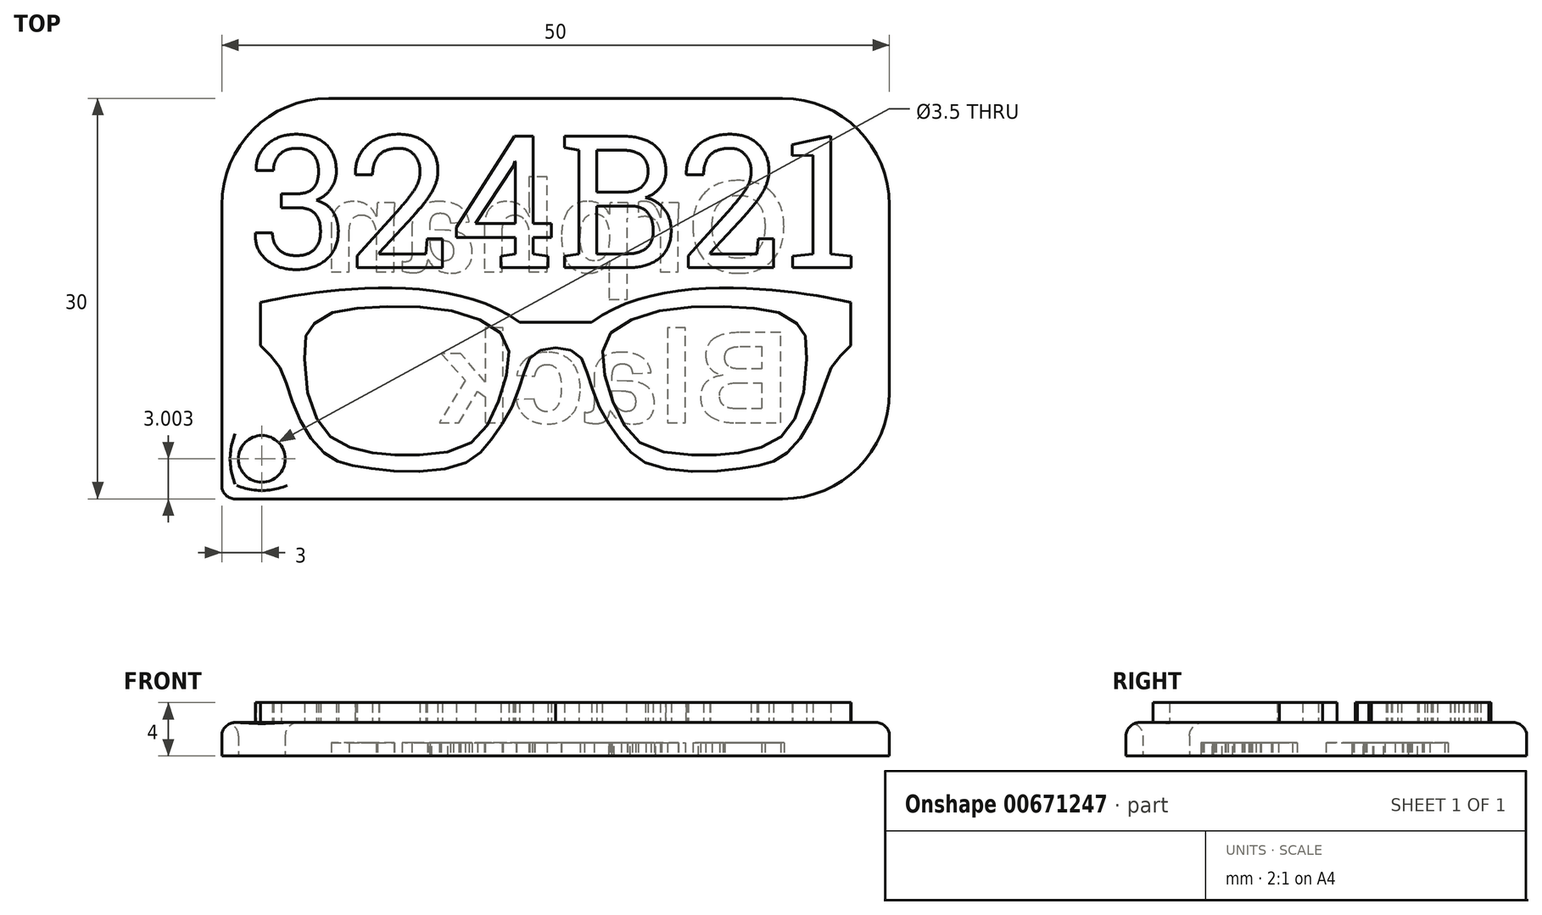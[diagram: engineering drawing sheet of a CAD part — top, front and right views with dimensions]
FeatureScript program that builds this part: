
annotation { "Feature Type Name" : "Feature", "Feature Type Description" : "" }
export const myFeature = defineFeature(function(context is Context, id is Id, definition is map)
    precondition{}
    {
        {
            var Q0;
            Q0=qCreatedBy(makeId("Top.planeOp"),FACE);
            var sketch = newSketch(context, id + "F0", { "sketchPlane" : qUnion([Q0])});
            skFitSpline(sketch, "E0", {"points": [v(2.9, -29.82) * mm, v(22.3, -31.3) * mm], "startDerivative": vector(6.49, 1.44) * mm, "endDerivative": vector(17.58, -13.11) * mm});
            skLineSegment(sketch, "E1", {"start": v(25, -66.67) * mm, "end": v(25, 0) * mm, "construction": true});
            skLineSegment(sketch, "E2", {"start": v(2.9, -29.82) * mm, "end": v(2.9, -33.05) * mm});
            skLineSegment(sketch, "E3", {"start": v(22.3, -31.3) * mm, "end": v(25, -31.3) * mm});
            skFitSpline(sketch, "E4", {"points": [v(2.9, -33.05) * mm, v(4.08, -34.28) * mm, v(4.97, -36.34) * mm, v(6.27, -39.38) * mm, v(8.2, -41.49) * mm, v(10.04, -42.06) * mm, v(13.88, -42.5) * mm, v(18.42, -41.75) * mm, v(20.07, -40.22) * mm, v(21.68, -37.74) * mm, v(22.6, -35.15) * mm, v(23.36, -33.67) * mm, v(25, -33.2) * mm], "startDerivative": vector(14.6, -17.1) * mm, "endDerivative": vector(27.6, 3.2) * mm});
            skFitSpline(sketch, "E5", {"points": [v(14.8, -41.25) * mm, v(17.8, -40.78) * mm, v(19.54, -39.5) * mm, v(20.74, -37.22) * mm, v(21.45, -34.5) * mm, v(21.28, -32.67) * mm, v(19.85, -31.38) * mm, v(16.73, -30.35) * mm, v(12.62, -30.13) * mm, v(9.28, -30.36) * mm, v(7.41, -31) * mm, v(6.45, -32) * mm, v(6.27, -32.53) * mm, v(6.34, -36.02) * mm, v(7.3, -38.87) * mm, v(8.6, -40.24) * mm, v(10.55, -40.94) * mm, v(12.58, -41.22) * mm, v(14.8, -41.25) * mm]});
            skLineSegment(sketch, "E6.MirrorCS", {"start": v(27.7, -31.3) * mm, "end": v(25, -31.3) * mm});
            skLineSegment(sketch, "E7.MirrorCS", {"start": v(47.1, -29.82) * mm, "end": v(47.1, -33.05) * mm});
            skFitSpline(sketch, "E8.MirrorC", {"points": [v(35.2, -41.25) * mm, v(32.2, -40.78) * mm, v(30.46, -39.5) * mm, v(29.26, -37.22) * mm, v(28.55, -34.5) * mm, v(28.72, -32.67) * mm, v(30.15, -31.38) * mm, v(33.27, -30.35) * mm, v(37.38, -30.13) * mm, v(40.72, -30.36) * mm, v(42.59, -31) * mm, v(43.55, -32) * mm, v(43.73, -32.53) * mm, v(43.66, -36.02) * mm, v(42.7, -38.87) * mm, v(41.4, -40.24) * mm, v(39.45, -40.94) * mm, v(37.42, -41.22) * mm, v(35.2, -41.25) * mm]});
            skFitSpline(sketch, "E9.MirrorCS", {"points": [v(47.1, -33.05) * mm, v(45.92, -34.28) * mm, v(45.03, -36.34) * mm, v(43.73, -39.38) * mm, v(41.8, -41.49) * mm, v(39.96, -42.06) * mm, v(36.12, -42.5) * mm, v(31.58, -41.75) * mm, v(29.93, -40.22) * mm, v(28.32, -37.74) * mm, v(27.4, -35.15) * mm, v(26.64, -33.67) * mm, v(25, -33.2) * mm], "startDerivative": vector(-14.6, -17.1) * mm, "endDerivative": vector(-27.6, 3.2) * mm});
            skFitSpline(sketch, "E10.MirrorCS", {"points": [v(47.1, -29.82) * mm, v(27.7, -31.3) * mm], "startDerivative": vector(-6.49, 1.44) * mm, "endDerivative": vector(-17.58, -13.11) * mm});
            skText(sketch, "E11", { "text": "324B21", "fontName": "RobotoSlab-Regular.ttf"});
            skLineSegment(sketch, "E12.bottom", {"start": v(0, -44.54) * mm, "end": v(50, -44.54) * mm});
            skLineSegment(sketch, "E12.top", {"start": v(0, -14.54) * mm, "end": v(50, -14.54) * mm});
            skLineSegment(sketch, "E12.left", {"start": v(0, -44.54) * mm, "end": v(0, -14.54) * mm});
            skLineSegment(sketch, "E12.right", {"start": v(50, -44.54) * mm, "end": v(50, -14.54) * mm});
            skCircle(sketch, "E13", {"center": v(3, -41.54) * mm, "radius": 1.75 * mm});
            const initialGuessF0  = {"E11": [0.002, -0.02722, 1, 0, 0.00998]};
            skSetInitialGuess(sketch, initialGuessF0);
            skSolve(sketch);
        }
        {
            var Q0;
            Q0=makeQuery(id+"F0.imprint","IMPRINT",FACE,{"disambiguationData":[TD([[makeQuery(id+"F0.imprint","IMPRINT",EDGE,{"derivedFrom":sQuery(id+"F0.wireOp",EDGE,"E0")}),1.0]])]});
            var Q1;
            Q1=makeQuery(id+"F0.imprint","IMPRINT",FACE,{"disambiguationData":[TD([[makeQuery(id+"F0.imprint","IMPRINT",EDGE,{"derivedFrom":sQuery(id+"F0.wireOp",EDGE,"E11.sketch_text.stroke-69")}),1.0]])]});
            var Q2;
            Q2=makeQuery(id+"F0.imprint","IMPRINT",FACE,{"disambiguationData":[TD([[makeQuery(id+"F0.imprint","IMPRINT",EDGE,{"derivedFrom":sQuery(id+"F0.wireOp",EDGE,"E11.sketch_text.stroke-97")}),1.0]])]});
            var Q3;
            Q3=makeQuery(id+"F0.imprint","IMPRINT",FACE,{"disambiguationData":[TD([[makeQuery(id+"F0.imprint","IMPRINT",EDGE,{"derivedFrom":sQuery(id+"F0.wireOp",EDGE,"E11.sketch_text.stroke-90")}),1.0]])]});
            var Q4;
            Q4=makeQuery(id+"F0.imprint","IMPRINT",FACE,{"disambiguationData":[TD([[makeQuery(id+"F0.imprint","IMPRINT",EDGE,{"derivedFrom":sQuery(id+"F0.wireOp",EDGE,"E8.MirrorC")}),-1.0]])]});
            var Q5;
            Q5=makeQuery(id+"F0.imprint","IMPRINT",FACE,{"disambiguationData":[TD([[makeQuery(id+"F0.imprint","IMPRINT",EDGE,{"derivedFrom":sQuery(id+"F0.wireOp",EDGE,"E5")}),1.0]])]});
            extrude(context, id + "F1", {"entities" : qUnion([Q0, Q1, Q2, Q3, Q4, Q5]), "depth" : 2.5 * mm, "offsetDistance" : 25 * mm});
        }
        {
            var Q0;
            Q0=makeQuery(id+"F0.imprint","IMPRINT",FACE,{"disambiguationData":[TD([[makeQuery(id+"F0.imprint","IMPRINT",EDGE,{"derivedFrom":sQuery(id+"F0.wireOp",EDGE,"E0")}),-1.0]])]});
            var Q1;
            Q1=makeQuery(id+"F0.imprint","IMPRINT",FACE,{"disambiguationData":[TD([[makeQuery(id+"F0.imprint","IMPRINT",EDGE,{"derivedFrom":sQuery(id+"F0.wireOp",EDGE,"E11.sketch_text.stroke-0")}),-1.0]])]});
            var Q2;
            Q2=makeQuery(id+"F0.imprint","IMPRINT",FACE,{"disambiguationData":[TD([[makeQuery(id+"F0.imprint","IMPRINT",EDGE,{"derivedFrom":sQuery(id+"F0.wireOp",EDGE,"E11.sketch_text.stroke-31")}),-1.0]])]});
            var Q3;
            Q3=makeQuery(id+"F0.imprint","IMPRINT",FACE,{"disambiguationData":[TD([[makeQuery(id+"F0.imprint","IMPRINT",EDGE,{"derivedFrom":sQuery(id+"F0.wireOp",EDGE,"E11.sketch_text.stroke-54")}),-1.0]])]});
            var Q4;
            Q4=makeQuery(id+"F0.imprint","IMPRINT",FACE,{"disambiguationData":[TD([[makeQuery(id+"F0.imprint","IMPRINT",EDGE,{"derivedFrom":sQuery(id+"F0.wireOp",EDGE,"E11.sketch_text.stroke-74")}),-1.0]])]});
            var Q5;
            Q5=makeQuery(id+"F0.imprint","IMPRINT",FACE,{"disambiguationData":[TD([[makeQuery(id+"F0.imprint","IMPRINT",EDGE,{"derivedFrom":sQuery(id+"F0.wireOp",EDGE,"E11.sketch_text.stroke-104")}),-1.0]])]});
            var Q6;
            Q6=makeQuery(id+"F0.imprint","IMPRINT",FACE,{"disambiguationData":[TD([[makeQuery(id+"F0.imprint","IMPRINT",EDGE,{"derivedFrom":sQuery(id+"F0.wireOp",EDGE,"E11.sketch_text.stroke-127")}),-1.0]])]});
            extrude(context, id + "F2", {"entities" : qUnion([Q0, Q1, Q2, Q3, Q4, Q5, Q6]), "operationType" : NewBodyOperationType.ADD, "depth" : 4 * mm, "offsetDistance" : 25 * mm});
        }
        {
            var Q0;
            Q0=makeQuery(id+"F1.opExtrude","SWEPT_EDGE",EDGE,{"disambiguationData":[OSD([sQuery(id+"F0.wireOp",EDGE,"E12.bottom"),sQuery(id+"F0.wireOp",EDGE,"E12.right")])]});
            var Q1;
            Q1=makeQuery(id+"F1.opExtrude","SWEPT_EDGE",EDGE,{"disambiguationData":[OSD([sQuery(id+"F0.wireOp",EDGE,"E12.top"),sQuery(id+"F0.wireOp",EDGE,"E12.right")])]});
            var Q2;
            Q2=makeQuery(id+"F1.opExtrude","SWEPT_EDGE",EDGE,{"disambiguationData":[OSD([sQuery(id+"F0.wireOp",EDGE,"E12.top"),sQuery(id+"F0.wireOp",EDGE,"E12.left")])]});
            fillet(context, id + "F3", {"entities" : qUnion([Q0, Q1, Q2]), "radius" : 8 * mm, "tangentPropagation" : true, "allowEdgeOverflow" : false});
        }
        {
            var Q0;
            Q0=makeQuery(id+"F1.opExtrude","SWEPT_EDGE",EDGE,{"disambiguationData":[OSD([sQuery(id+"F0.wireOp",EDGE,"E12.bottom"),sQuery(id+"F0.wireOp",EDGE,"E12.left")])]});
            var Q1;
            Q1=makeQuery(id+"F1.opExtrude","CAP_EDGE",EDGE,{"disambiguationData":[OSD([sQuery(id+"F0.wireOp",EDGE,"E12.bottom")])],"isStart":false});
            var Q2;
            Q2=makeQuery(id+"F1.opExtrude","CAP_EDGE",EDGE,{"disambiguationData":[OSD([sQuery(id+"F0.wireOp",EDGE,"E12.left")])],"isStart":false});
            var Q3;
            Q3=makeQuery(id+"F1.opExtrude","CAP_EDGE",EDGE,{"disambiguationData":[OSD([sQuery(id+"F0.wireOp",EDGE,"E13")])],"isStart":false});
            var Q4;
            {var subQ0=sQuery(id+"F0.wireOp",EDGE,"E12.left");var subQ1=sQuery(id+"F0.wireOp",EDGE,"E12.top");Q4=makeQuery(id+"F3.opFillet","BLEND_EDGE",EDGE,{"blendedFrom":[makeQuery(id+"F1.opExtrude","SWEPT_EDGE",EDGE,{"disambiguationData":[OSD([subQ1,subQ0])]}),makeQuery(id+"F1.opExtrude","CAP_FACE",FACE,{"disambiguationData":[OSD([sQuery(id+"F0.wireOp",EDGE,"E0"),sQuery(id+"F0.wireOp",EDGE,"E2"),sQuery(id+"F0.wireOp",EDGE,"E3"),sQuery(id+"F0.wireOp",EDGE,"E4"),sQuery(id+"F0.wireOp",EDGE,"E6.MirrorCS"),sQuery(id+"F0.wireOp",EDGE,"E7.MirrorCS"),sQuery(id+"F0.wireOp",EDGE,"E9.MirrorCS"),sQuery(id+"F0.wireOp",EDGE,"E10.MirrorCS"),sQuery(id+"F0.wireOp",EDGE,"E11.sketch_text.stroke-0"),sQuery(id+"F0.wireOp",EDGE,"E11.sketch_text.stroke-1"),sQuery(id+"F0.wireOp",EDGE,"E11.sketch_text.stroke-2"),sQuery(id+"F0.wireOp",EDGE,"E11.sketch_text.stroke-3"),sQuery(id+"F0.wireOp",EDGE,"E11.sketch_text.stroke-4"),sQuery(id+"F0.wireOp",EDGE,"E11.sketch_text.stroke-5"),sQuery(id+"F0.wireOp",EDGE,"E11.sketch_text.stroke-6"),sQuery(id+"F0.wireOp",EDGE,"E11.sketch_text.stroke-7"),sQuery(id+"F0.wireOp",EDGE,"E11.sketch_text.stroke-8"),sQuery(id+"F0.wireOp",EDGE,"E11.sketch_text.stroke-9"),sQuery(id+"F0.wireOp",EDGE,"E11.sketch_text.stroke-10"),sQuery(id+"F0.wireOp",EDGE,"E11.sketch_text.stroke-11"),sQuery(id+"F0.wireOp",EDGE,"E11.sketch_text.stroke-12"),sQuery(id+"F0.wireOp",EDGE,"E11.sketch_text.stroke-13"),sQuery(id+"F0.wireOp",EDGE,"E11.sketch_text.stroke-14"),sQuery(id+"F0.wireOp",EDGE,"E11.sketch_text.stroke-15"),sQuery(id+"F0.wireOp",EDGE,"E11.sketch_text.stroke-16"),sQuery(id+"F0.wireOp",EDGE,"E11.sketch_text.stroke-17"),sQuery(id+"F0.wireOp",EDGE,"E11.sketch_text.stroke-18"),sQuery(id+"F0.wireOp",EDGE,"E11.sketch_text.stroke-19"),sQuery(id+"F0.wireOp",EDGE,"E11.sketch_text.stroke-20"),sQuery(id+"F0.wireOp",EDGE,"E11.sketch_text.stroke-21"),sQuery(id+"F0.wireOp",EDGE,"E11.sketch_text.stroke-22"),sQuery(id+"F0.wireOp",EDGE,"E11.sketch_text.stroke-23"),sQuery(id+"F0.wireOp",EDGE,"E11.sketch_text.stroke-24"),sQuery(id+"F0.wireOp",EDGE,"E11.sketch_text.stroke-25"),sQuery(id+"F0.wireOp",EDGE,"E11.sketch_text.stroke-26"),sQuery(id+"F0.wireOp",EDGE,"E11.sketch_text.stroke-27"),sQuery(id+"F0.wireOp",EDGE,"E11.sketch_text.stroke-28"),sQuery(id+"F0.wireOp",EDGE,"E11.sketch_text.stroke-29"),sQuery(id+"F0.wireOp",EDGE,"E11.sketch_text.stroke-30"),sQuery(id+"F0.wireOp",EDGE,"E11.sketch_text.stroke-31"),sQuery(id+"F0.wireOp",EDGE,"E11.sketch_text.stroke-32"),sQuery(id+"F0.wireOp",EDGE,"E11.sketch_text.stroke-33"),sQuery(id+"F0.wireOp",EDGE,"E11.sketch_text.stroke-34"),sQuery(id+"F0.wireOp",EDGE,"E11.sketch_text.stroke-35"),sQuery(id+"F0.wireOp",EDGE,"E11.sketch_text.stroke-36"),sQuery(id+"F0.wireOp",EDGE,"E11.sketch_text.stroke-37"),sQuery(id+"F0.wireOp",EDGE,"E11.sketch_text.stroke-38"),sQuery(id+"F0.wireOp",EDGE,"E11.sketch_text.stroke-39"),sQuery(id+"F0.wireOp",EDGE,"E11.sketch_text.stroke-40"),sQuery(id+"F0.wireOp",EDGE,"E11.sketch_text.stroke-41"),sQuery(id+"F0.wireOp",EDGE,"E11.sketch_text.stroke-42"),sQuery(id+"F0.wireOp",EDGE,"E11.sketch_text.stroke-43"),sQuery(id+"F0.wireOp",EDGE,"E11.sketch_text.stroke-44"),sQuery(id+"F0.wireOp",EDGE,"E11.sketch_text.stroke-45"),sQuery(id+"F0.wireOp",EDGE,"E11.sketch_text.stroke-46"),sQuery(id+"F0.wireOp",EDGE,"E11.sketch_text.stroke-47"),sQuery(id+"F0.wireOp",EDGE,"E11.sketch_text.stroke-48"),sQuery(id+"F0.wireOp",EDGE,"E11.sketch_text.stroke-49"),sQuery(id+"F0.wireOp",EDGE,"E11.sketch_text.stroke-50"),sQuery(id+"F0.wireOp",EDGE,"E11.sketch_text.stroke-51"),sQuery(id+"F0.wireOp",EDGE,"E11.sketch_text.stroke-52"),sQuery(id+"F0.wireOp",EDGE,"E11.sketch_text.stroke-53"),sQuery(id+"F0.wireOp",EDGE,"E11.sketch_text.stroke-54"),sQuery(id+"F0.wireOp",EDGE,"E11.sketch_text.stroke-55"),sQuery(id+"F0.wireOp",EDGE,"E11.sketch_text.stroke-56"),sQuery(id+"F0.wireOp",EDGE,"E11.sketch_text.stroke-57"),sQuery(id+"F0.wireOp",EDGE,"E11.sketch_text.stroke-58"),sQuery(id+"F0.wireOp",EDGE,"E11.sketch_text.stroke-59"),sQuery(id+"F0.wireOp",EDGE,"E11.sketch_text.stroke-60"),sQuery(id+"F0.wireOp",EDGE,"E11.sketch_text.stroke-61"),sQuery(id+"F0.wireOp",EDGE,"E11.sketch_text.stroke-62"),sQuery(id+"F0.wireOp",EDGE,"E11.sketch_text.stroke-63"),sQuery(id+"F0.wireOp",EDGE,"E11.sketch_text.stroke-64"),sQuery(id+"F0.wireOp",EDGE,"E11.sketch_text.stroke-65"),sQuery(id+"F0.wireOp",EDGE,"E11.sketch_text.stroke-66"),sQuery(id+"F0.wireOp",EDGE,"E11.sketch_text.stroke-67"),sQuery(id+"F0.wireOp",EDGE,"E11.sketch_text.stroke-68"),sQuery(id+"F0.wireOp",EDGE,"E11.sketch_text.stroke-74"),sQuery(id+"F0.wireOp",EDGE,"E11.sketch_text.stroke-75"),sQuery(id+"F0.wireOp",EDGE,"E11.sketch_text.stroke-76"),sQuery(id+"F0.wireOp",EDGE,"E11.sketch_text.stroke-77"),sQuery(id+"F0.wireOp",EDGE,"E11.sketch_text.stroke-78"),sQuery(id+"F0.wireOp",EDGE,"E11.sketch_text.stroke-79"),sQuery(id+"F0.wireOp",EDGE,"E11.sketch_text.stroke-80"),sQuery(id+"F0.wireOp",EDGE,"E11.sketch_text.stroke-81"),sQuery(id+"F0.wireOp",EDGE,"E11.sketch_text.stroke-82"),sQuery(id+"F0.wireOp",EDGE,"E11.sketch_text.stroke-83"),sQuery(id+"F0.wireOp",EDGE,"E11.sketch_text.stroke-84"),sQuery(id+"F0.wireOp",EDGE,"E11.sketch_text.stroke-85"),sQuery(id+"F0.wireOp",EDGE,"E11.sketch_text.stroke-86"),sQuery(id+"F0.wireOp",EDGE,"E11.sketch_text.stroke-87"),sQuery(id+"F0.wireOp",EDGE,"E11.sketch_text.stroke-88"),sQuery(id+"F0.wireOp",EDGE,"E11.sketch_text.stroke-89"),sQuery(id+"F0.wireOp",EDGE,"E11.sketch_text.stroke-104"),sQuery(id+"F0.wireOp",EDGE,"E11.sketch_text.stroke-105"),sQuery(id+"F0.wireOp",EDGE,"E11.sketch_text.stroke-106"),sQuery(id+"F0.wireOp",EDGE,"E11.sketch_text.stroke-107"),sQuery(id+"F0.wireOp",EDGE,"E11.sketch_text.stroke-108"),sQuery(id+"F0.wireOp",EDGE,"E11.sketch_text.stroke-109"),sQuery(id+"F0.wireOp",EDGE,"E11.sketch_text.stroke-110"),sQuery(id+"F0.wireOp",EDGE,"E11.sketch_text.stroke-111"),sQuery(id+"F0.wireOp",EDGE,"E11.sketch_text.stroke-112"),sQuery(id+"F0.wireOp",EDGE,"E11.sketch_text.stroke-113"),sQuery(id+"F0.wireOp",EDGE,"E11.sketch_text.stroke-114"),sQuery(id+"F0.wireOp",EDGE,"E11.sketch_text.stroke-115"),sQuery(id+"F0.wireOp",EDGE,"E11.sketch_text.stroke-116"),sQuery(id+"F0.wireOp",EDGE,"E11.sketch_text.stroke-117"),sQuery(id+"F0.wireOp",EDGE,"E11.sketch_text.stroke-118"),sQuery(id+"F0.wireOp",EDGE,"E11.sketch_text.stroke-119"),sQuery(id+"F0.wireOp",EDGE,"E11.sketch_text.stroke-120"),sQuery(id+"F0.wireOp",EDGE,"E11.sketch_text.stroke-121"),sQuery(id+"F0.wireOp",EDGE,"E11.sketch_text.stroke-122"),sQuery(id+"F0.wireOp",EDGE,"E11.sketch_text.stroke-123"),sQuery(id+"F0.wireOp",EDGE,"E11.sketch_text.stroke-124"),sQuery(id+"F0.wireOp",EDGE,"E11.sketch_text.stroke-125"),sQuery(id+"F0.wireOp",EDGE,"E11.sketch_text.stroke-126"),sQuery(id+"F0.wireOp",EDGE,"E11.sketch_text.stroke-127"),sQuery(id+"F0.wireOp",EDGE,"E11.sketch_text.stroke-128"),sQuery(id+"F0.wireOp",EDGE,"E11.sketch_text.stroke-129"),sQuery(id+"F0.wireOp",EDGE,"E11.sketch_text.stroke-130"),sQuery(id+"F0.wireOp",EDGE,"E11.sketch_text.stroke-131"),sQuery(id+"F0.wireOp",EDGE,"E11.sketch_text.stroke-132"),sQuery(id+"F0.wireOp",EDGE,"E11.sketch_text.stroke-133"),sQuery(id+"F0.wireOp",EDGE,"E11.sketch_text.stroke-134"),sQuery(id+"F0.wireOp",EDGE,"E11.sketch_text.stroke-135"),sQuery(id+"F0.wireOp",EDGE,"E11.sketch_text.stroke-136"),sQuery(id+"F0.wireOp",EDGE,"E12.bottom"),subQ1,subQ0,sQuery(id+"F0.wireOp",EDGE,"E12.right"),sQuery(id+"F0.wireOp",EDGE,"E13")])],"isStart":false})],"blendedInto":[makeQuery(id+"F1.opExtrude","CAP_FACE",FACE,{"disambiguationData":[OSD([sQuery(id+"F0.wireOp",EDGE,"E0"),sQuery(id+"F0.wireOp",EDGE,"E2"),sQuery(id+"F0.wireOp",EDGE,"E3"),sQuery(id+"F0.wireOp",EDGE,"E4"),sQuery(id+"F0.wireOp",EDGE,"E6.MirrorCS"),sQuery(id+"F0.wireOp",EDGE,"E7.MirrorCS"),sQuery(id+"F0.wireOp",EDGE,"E9.MirrorCS"),sQuery(id+"F0.wireOp",EDGE,"E10.MirrorCS"),sQuery(id+"F0.wireOp",EDGE,"E11.sketch_text.stroke-0"),sQuery(id+"F0.wireOp",EDGE,"E11.sketch_text.stroke-1"),sQuery(id+"F0.wireOp",EDGE,"E11.sketch_text.stroke-2"),sQuery(id+"F0.wireOp",EDGE,"E11.sketch_text.stroke-3"),sQuery(id+"F0.wireOp",EDGE,"E11.sketch_text.stroke-4"),sQuery(id+"F0.wireOp",EDGE,"E11.sketch_text.stroke-5"),sQuery(id+"F0.wireOp",EDGE,"E11.sketch_text.stroke-6"),sQuery(id+"F0.wireOp",EDGE,"E11.sketch_text.stroke-7"),sQuery(id+"F0.wireOp",EDGE,"E11.sketch_text.stroke-8"),sQuery(id+"F0.wireOp",EDGE,"E11.sketch_text.stroke-9"),sQuery(id+"F0.wireOp",EDGE,"E11.sketch_text.stroke-10"),sQuery(id+"F0.wireOp",EDGE,"E11.sketch_text.stroke-11"),sQuery(id+"F0.wireOp",EDGE,"E11.sketch_text.stroke-12"),sQuery(id+"F0.wireOp",EDGE,"E11.sketch_text.stroke-13"),sQuery(id+"F0.wireOp",EDGE,"E11.sketch_text.stroke-14"),sQuery(id+"F0.wireOp",EDGE,"E11.sketch_text.stroke-15"),sQuery(id+"F0.wireOp",EDGE,"E11.sketch_text.stroke-16"),sQuery(id+"F0.wireOp",EDGE,"E11.sketch_text.stroke-17"),sQuery(id+"F0.wireOp",EDGE,"E11.sketch_text.stroke-18"),sQuery(id+"F0.wireOp",EDGE,"E11.sketch_text.stroke-19"),sQuery(id+"F0.wireOp",EDGE,"E11.sketch_text.stroke-20"),sQuery(id+"F0.wireOp",EDGE,"E11.sketch_text.stroke-21"),sQuery(id+"F0.wireOp",EDGE,"E11.sketch_text.stroke-22"),sQuery(id+"F0.wireOp",EDGE,"E11.sketch_text.stroke-23"),sQuery(id+"F0.wireOp",EDGE,"E11.sketch_text.stroke-24"),sQuery(id+"F0.wireOp",EDGE,"E11.sketch_text.stroke-25"),sQuery(id+"F0.wireOp",EDGE,"E11.sketch_text.stroke-26"),sQuery(id+"F0.wireOp",EDGE,"E11.sketch_text.stroke-27"),sQuery(id+"F0.wireOp",EDGE,"E11.sketch_text.stroke-28"),sQuery(id+"F0.wireOp",EDGE,"E11.sketch_text.stroke-29"),sQuery(id+"F0.wireOp",EDGE,"E11.sketch_text.stroke-30"),sQuery(id+"F0.wireOp",EDGE,"E11.sketch_text.stroke-31"),sQuery(id+"F0.wireOp",EDGE,"E11.sketch_text.stroke-32"),sQuery(id+"F0.wireOp",EDGE,"E11.sketch_text.stroke-33"),sQuery(id+"F0.wireOp",EDGE,"E11.sketch_text.stroke-34"),sQuery(id+"F0.wireOp",EDGE,"E11.sketch_text.stroke-35"),sQuery(id+"F0.wireOp",EDGE,"E11.sketch_text.stroke-36"),sQuery(id+"F0.wireOp",EDGE,"E11.sketch_text.stroke-37"),sQuery(id+"F0.wireOp",EDGE,"E11.sketch_text.stroke-38"),sQuery(id+"F0.wireOp",EDGE,"E11.sketch_text.stroke-39"),sQuery(id+"F0.wireOp",EDGE,"E11.sketch_text.stroke-40"),sQuery(id+"F0.wireOp",EDGE,"E11.sketch_text.stroke-41"),sQuery(id+"F0.wireOp",EDGE,"E11.sketch_text.stroke-42"),sQuery(id+"F0.wireOp",EDGE,"E11.sketch_text.stroke-43"),sQuery(id+"F0.wireOp",EDGE,"E11.sketch_text.stroke-44"),sQuery(id+"F0.wireOp",EDGE,"E11.sketch_text.stroke-45"),sQuery(id+"F0.wireOp",EDGE,"E11.sketch_text.stroke-46"),sQuery(id+"F0.wireOp",EDGE,"E11.sketch_text.stroke-47"),sQuery(id+"F0.wireOp",EDGE,"E11.sketch_text.stroke-48"),sQuery(id+"F0.wireOp",EDGE,"E11.sketch_text.stroke-49"),sQuery(id+"F0.wireOp",EDGE,"E11.sketch_text.stroke-50"),sQuery(id+"F0.wireOp",EDGE,"E11.sketch_text.stroke-51"),sQuery(id+"F0.wireOp",EDGE,"E11.sketch_text.stroke-52"),sQuery(id+"F0.wireOp",EDGE,"E11.sketch_text.stroke-53"),sQuery(id+"F0.wireOp",EDGE,"E11.sketch_text.stroke-54"),sQuery(id+"F0.wireOp",EDGE,"E11.sketch_text.stroke-55"),sQuery(id+"F0.wireOp",EDGE,"E11.sketch_text.stroke-56"),sQuery(id+"F0.wireOp",EDGE,"E11.sketch_text.stroke-57"),sQuery(id+"F0.wireOp",EDGE,"E11.sketch_text.stroke-58"),sQuery(id+"F0.wireOp",EDGE,"E11.sketch_text.stroke-59"),sQuery(id+"F0.wireOp",EDGE,"E11.sketch_text.stroke-60"),sQuery(id+"F0.wireOp",EDGE,"E11.sketch_text.stroke-61"),sQuery(id+"F0.wireOp",EDGE,"E11.sketch_text.stroke-62"),sQuery(id+"F0.wireOp",EDGE,"E11.sketch_text.stroke-63"),sQuery(id+"F0.wireOp",EDGE,"E11.sketch_text.stroke-64"),sQuery(id+"F0.wireOp",EDGE,"E11.sketch_text.stroke-65"),sQuery(id+"F0.wireOp",EDGE,"E11.sketch_text.stroke-66"),sQuery(id+"F0.wireOp",EDGE,"E11.sketch_text.stroke-67"),sQuery(id+"F0.wireOp",EDGE,"E11.sketch_text.stroke-68"),sQuery(id+"F0.wireOp",EDGE,"E11.sketch_text.stroke-74"),sQuery(id+"F0.wireOp",EDGE,"E11.sketch_text.stroke-75"),sQuery(id+"F0.wireOp",EDGE,"E11.sketch_text.stroke-76"),sQuery(id+"F0.wireOp",EDGE,"E11.sketch_text.stroke-77"),sQuery(id+"F0.wireOp",EDGE,"E11.sketch_text.stroke-78"),sQuery(id+"F0.wireOp",EDGE,"E11.sketch_text.stroke-79"),sQuery(id+"F0.wireOp",EDGE,"E11.sketch_text.stroke-80"),sQuery(id+"F0.wireOp",EDGE,"E11.sketch_text.stroke-81"),sQuery(id+"F0.wireOp",EDGE,"E11.sketch_text.stroke-82"),sQuery(id+"F0.wireOp",EDGE,"E11.sketch_text.stroke-83"),sQuery(id+"F0.wireOp",EDGE,"E11.sketch_text.stroke-84"),sQuery(id+"F0.wireOp",EDGE,"E11.sketch_text.stroke-85"),sQuery(id+"F0.wireOp",EDGE,"E11.sketch_text.stroke-86"),sQuery(id+"F0.wireOp",EDGE,"E11.sketch_text.stroke-87"),sQuery(id+"F0.wireOp",EDGE,"E11.sketch_text.stroke-88"),sQuery(id+"F0.wireOp",EDGE,"E11.sketch_text.stroke-89"),sQuery(id+"F0.wireOp",EDGE,"E11.sketch_text.stroke-104"),sQuery(id+"F0.wireOp",EDGE,"E11.sketch_text.stroke-105"),sQuery(id+"F0.wireOp",EDGE,"E11.sketch_text.stroke-106"),sQuery(id+"F0.wireOp",EDGE,"E11.sketch_text.stroke-107"),sQuery(id+"F0.wireOp",EDGE,"E11.sketch_text.stroke-108"),sQuery(id+"F0.wireOp",EDGE,"E11.sketch_text.stroke-109"),sQuery(id+"F0.wireOp",EDGE,"E11.sketch_text.stroke-110"),sQuery(id+"F0.wireOp",EDGE,"E11.sketch_text.stroke-111"),sQuery(id+"F0.wireOp",EDGE,"E11.sketch_text.stroke-112"),sQuery(id+"F0.wireOp",EDGE,"E11.sketch_text.stroke-113"),sQuery(id+"F0.wireOp",EDGE,"E11.sketch_text.stroke-114"),sQuery(id+"F0.wireOp",EDGE,"E11.sketch_text.stroke-115"),sQuery(id+"F0.wireOp",EDGE,"E11.sketch_text.stroke-116"),sQuery(id+"F0.wireOp",EDGE,"E11.sketch_text.stroke-117"),sQuery(id+"F0.wireOp",EDGE,"E11.sketch_text.stroke-118"),sQuery(id+"F0.wireOp",EDGE,"E11.sketch_text.stroke-119"),sQuery(id+"F0.wireOp",EDGE,"E11.sketch_text.stroke-120"),sQuery(id+"F0.wireOp",EDGE,"E11.sketch_text.stroke-121"),sQuery(id+"F0.wireOp",EDGE,"E11.sketch_text.stroke-122"),sQuery(id+"F0.wireOp",EDGE,"E11.sketch_text.stroke-123"),sQuery(id+"F0.wireOp",EDGE,"E11.sketch_text.stroke-124"),sQuery(id+"F0.wireOp",EDGE,"E11.sketch_text.stroke-125"),sQuery(id+"F0.wireOp",EDGE,"E11.sketch_text.stroke-126"),sQuery(id+"F0.wireOp",EDGE,"E11.sketch_text.stroke-127"),sQuery(id+"F0.wireOp",EDGE,"E11.sketch_text.stroke-128"),sQuery(id+"F0.wireOp",EDGE,"E11.sketch_text.stroke-129"),sQuery(id+"F0.wireOp",EDGE,"E11.sketch_text.stroke-130"),sQuery(id+"F0.wireOp",EDGE,"E11.sketch_text.stroke-131"),sQuery(id+"F0.wireOp",EDGE,"E11.sketch_text.stroke-132"),sQuery(id+"F0.wireOp",EDGE,"E11.sketch_text.stroke-133"),sQuery(id+"F0.wireOp",EDGE,"E11.sketch_text.stroke-134"),sQuery(id+"F0.wireOp",EDGE,"E11.sketch_text.stroke-135"),sQuery(id+"F0.wireOp",EDGE,"E11.sketch_text.stroke-136"),sQuery(id+"F0.wireOp",EDGE,"E12.bottom"),subQ1,subQ0,sQuery(id+"F0.wireOp",EDGE,"E12.right"),sQuery(id+"F0.wireOp",EDGE,"E13")])],"isStart":false})]});}
            var Q5;
            Q5=makeQuery(id+"F1.opExtrude","CAP_EDGE",EDGE,{"disambiguationData":[OSD([sQuery(id+"F0.wireOp",EDGE,"E12.top")])],"isStart":false});
            var Q6;
            {var subQ0=sQuery(id+"F0.wireOp",EDGE,"E12.right");var subQ1=sQuery(id+"F0.wireOp",EDGE,"E12.top");Q6=makeQuery(id+"F3.opFillet","BLEND_EDGE",EDGE,{"blendedFrom":[makeQuery(id+"F1.opExtrude","SWEPT_EDGE",EDGE,{"disambiguationData":[OSD([subQ1,subQ0])]}),makeQuery(id+"F1.opExtrude","CAP_FACE",FACE,{"disambiguationData":[OSD([sQuery(id+"F0.wireOp",EDGE,"E0"),sQuery(id+"F0.wireOp",EDGE,"E2"),sQuery(id+"F0.wireOp",EDGE,"E3"),sQuery(id+"F0.wireOp",EDGE,"E4"),sQuery(id+"F0.wireOp",EDGE,"E6.MirrorCS"),sQuery(id+"F0.wireOp",EDGE,"E7.MirrorCS"),sQuery(id+"F0.wireOp",EDGE,"E9.MirrorCS"),sQuery(id+"F0.wireOp",EDGE,"E10.MirrorCS"),sQuery(id+"F0.wireOp",EDGE,"E11.sketch_text.stroke-0"),sQuery(id+"F0.wireOp",EDGE,"E11.sketch_text.stroke-1"),sQuery(id+"F0.wireOp",EDGE,"E11.sketch_text.stroke-2"),sQuery(id+"F0.wireOp",EDGE,"E11.sketch_text.stroke-3"),sQuery(id+"F0.wireOp",EDGE,"E11.sketch_text.stroke-4"),sQuery(id+"F0.wireOp",EDGE,"E11.sketch_text.stroke-5"),sQuery(id+"F0.wireOp",EDGE,"E11.sketch_text.stroke-6"),sQuery(id+"F0.wireOp",EDGE,"E11.sketch_text.stroke-7"),sQuery(id+"F0.wireOp",EDGE,"E11.sketch_text.stroke-8"),sQuery(id+"F0.wireOp",EDGE,"E11.sketch_text.stroke-9"),sQuery(id+"F0.wireOp",EDGE,"E11.sketch_text.stroke-10"),sQuery(id+"F0.wireOp",EDGE,"E11.sketch_text.stroke-11"),sQuery(id+"F0.wireOp",EDGE,"E11.sketch_text.stroke-12"),sQuery(id+"F0.wireOp",EDGE,"E11.sketch_text.stroke-13"),sQuery(id+"F0.wireOp",EDGE,"E11.sketch_text.stroke-14"),sQuery(id+"F0.wireOp",EDGE,"E11.sketch_text.stroke-15"),sQuery(id+"F0.wireOp",EDGE,"E11.sketch_text.stroke-16"),sQuery(id+"F0.wireOp",EDGE,"E11.sketch_text.stroke-17"),sQuery(id+"F0.wireOp",EDGE,"E11.sketch_text.stroke-18"),sQuery(id+"F0.wireOp",EDGE,"E11.sketch_text.stroke-19"),sQuery(id+"F0.wireOp",EDGE,"E11.sketch_text.stroke-20"),sQuery(id+"F0.wireOp",EDGE,"E11.sketch_text.stroke-21"),sQuery(id+"F0.wireOp",EDGE,"E11.sketch_text.stroke-22"),sQuery(id+"F0.wireOp",EDGE,"E11.sketch_text.stroke-23"),sQuery(id+"F0.wireOp",EDGE,"E11.sketch_text.stroke-24"),sQuery(id+"F0.wireOp",EDGE,"E11.sketch_text.stroke-25"),sQuery(id+"F0.wireOp",EDGE,"E11.sketch_text.stroke-26"),sQuery(id+"F0.wireOp",EDGE,"E11.sketch_text.stroke-27"),sQuery(id+"F0.wireOp",EDGE,"E11.sketch_text.stroke-28"),sQuery(id+"F0.wireOp",EDGE,"E11.sketch_text.stroke-29"),sQuery(id+"F0.wireOp",EDGE,"E11.sketch_text.stroke-30"),sQuery(id+"F0.wireOp",EDGE,"E11.sketch_text.stroke-31"),sQuery(id+"F0.wireOp",EDGE,"E11.sketch_text.stroke-32"),sQuery(id+"F0.wireOp",EDGE,"E11.sketch_text.stroke-33"),sQuery(id+"F0.wireOp",EDGE,"E11.sketch_text.stroke-34"),sQuery(id+"F0.wireOp",EDGE,"E11.sketch_text.stroke-35"),sQuery(id+"F0.wireOp",EDGE,"E11.sketch_text.stroke-36"),sQuery(id+"F0.wireOp",EDGE,"E11.sketch_text.stroke-37"),sQuery(id+"F0.wireOp",EDGE,"E11.sketch_text.stroke-38"),sQuery(id+"F0.wireOp",EDGE,"E11.sketch_text.stroke-39"),sQuery(id+"F0.wireOp",EDGE,"E11.sketch_text.stroke-40"),sQuery(id+"F0.wireOp",EDGE,"E11.sketch_text.stroke-41"),sQuery(id+"F0.wireOp",EDGE,"E11.sketch_text.stroke-42"),sQuery(id+"F0.wireOp",EDGE,"E11.sketch_text.stroke-43"),sQuery(id+"F0.wireOp",EDGE,"E11.sketch_text.stroke-44"),sQuery(id+"F0.wireOp",EDGE,"E11.sketch_text.stroke-45"),sQuery(id+"F0.wireOp",EDGE,"E11.sketch_text.stroke-46"),sQuery(id+"F0.wireOp",EDGE,"E11.sketch_text.stroke-47"),sQuery(id+"F0.wireOp",EDGE,"E11.sketch_text.stroke-48"),sQuery(id+"F0.wireOp",EDGE,"E11.sketch_text.stroke-49"),sQuery(id+"F0.wireOp",EDGE,"E11.sketch_text.stroke-50"),sQuery(id+"F0.wireOp",EDGE,"E11.sketch_text.stroke-51"),sQuery(id+"F0.wireOp",EDGE,"E11.sketch_text.stroke-52"),sQuery(id+"F0.wireOp",EDGE,"E11.sketch_text.stroke-53"),sQuery(id+"F0.wireOp",EDGE,"E11.sketch_text.stroke-54"),sQuery(id+"F0.wireOp",EDGE,"E11.sketch_text.stroke-55"),sQuery(id+"F0.wireOp",EDGE,"E11.sketch_text.stroke-56"),sQuery(id+"F0.wireOp",EDGE,"E11.sketch_text.stroke-57"),sQuery(id+"F0.wireOp",EDGE,"E11.sketch_text.stroke-58"),sQuery(id+"F0.wireOp",EDGE,"E11.sketch_text.stroke-59"),sQuery(id+"F0.wireOp",EDGE,"E11.sketch_text.stroke-60"),sQuery(id+"F0.wireOp",EDGE,"E11.sketch_text.stroke-61"),sQuery(id+"F0.wireOp",EDGE,"E11.sketch_text.stroke-62"),sQuery(id+"F0.wireOp",EDGE,"E11.sketch_text.stroke-63"),sQuery(id+"F0.wireOp",EDGE,"E11.sketch_text.stroke-64"),sQuery(id+"F0.wireOp",EDGE,"E11.sketch_text.stroke-65"),sQuery(id+"F0.wireOp",EDGE,"E11.sketch_text.stroke-66"),sQuery(id+"F0.wireOp",EDGE,"E11.sketch_text.stroke-67"),sQuery(id+"F0.wireOp",EDGE,"E11.sketch_text.stroke-68"),sQuery(id+"F0.wireOp",EDGE,"E11.sketch_text.stroke-74"),sQuery(id+"F0.wireOp",EDGE,"E11.sketch_text.stroke-75"),sQuery(id+"F0.wireOp",EDGE,"E11.sketch_text.stroke-76"),sQuery(id+"F0.wireOp",EDGE,"E11.sketch_text.stroke-77"),sQuery(id+"F0.wireOp",EDGE,"E11.sketch_text.stroke-78"),sQuery(id+"F0.wireOp",EDGE,"E11.sketch_text.stroke-79"),sQuery(id+"F0.wireOp",EDGE,"E11.sketch_text.stroke-80"),sQuery(id+"F0.wireOp",EDGE,"E11.sketch_text.stroke-81"),sQuery(id+"F0.wireOp",EDGE,"E11.sketch_text.stroke-82"),sQuery(id+"F0.wireOp",EDGE,"E11.sketch_text.stroke-83"),sQuery(id+"F0.wireOp",EDGE,"E11.sketch_text.stroke-84"),sQuery(id+"F0.wireOp",EDGE,"E11.sketch_text.stroke-85"),sQuery(id+"F0.wireOp",EDGE,"E11.sketch_text.stroke-86"),sQuery(id+"F0.wireOp",EDGE,"E11.sketch_text.stroke-87"),sQuery(id+"F0.wireOp",EDGE,"E11.sketch_text.stroke-88"),sQuery(id+"F0.wireOp",EDGE,"E11.sketch_text.stroke-89"),sQuery(id+"F0.wireOp",EDGE,"E11.sketch_text.stroke-104"),sQuery(id+"F0.wireOp",EDGE,"E11.sketch_text.stroke-105"),sQuery(id+"F0.wireOp",EDGE,"E11.sketch_text.stroke-106"),sQuery(id+"F0.wireOp",EDGE,"E11.sketch_text.stroke-107"),sQuery(id+"F0.wireOp",EDGE,"E11.sketch_text.stroke-108"),sQuery(id+"F0.wireOp",EDGE,"E11.sketch_text.stroke-109"),sQuery(id+"F0.wireOp",EDGE,"E11.sketch_text.stroke-110"),sQuery(id+"F0.wireOp",EDGE,"E11.sketch_text.stroke-111"),sQuery(id+"F0.wireOp",EDGE,"E11.sketch_text.stroke-112"),sQuery(id+"F0.wireOp",EDGE,"E11.sketch_text.stroke-113"),sQuery(id+"F0.wireOp",EDGE,"E11.sketch_text.stroke-114"),sQuery(id+"F0.wireOp",EDGE,"E11.sketch_text.stroke-115"),sQuery(id+"F0.wireOp",EDGE,"E11.sketch_text.stroke-116"),sQuery(id+"F0.wireOp",EDGE,"E11.sketch_text.stroke-117"),sQuery(id+"F0.wireOp",EDGE,"E11.sketch_text.stroke-118"),sQuery(id+"F0.wireOp",EDGE,"E11.sketch_text.stroke-119"),sQuery(id+"F0.wireOp",EDGE,"E11.sketch_text.stroke-120"),sQuery(id+"F0.wireOp",EDGE,"E11.sketch_text.stroke-121"),sQuery(id+"F0.wireOp",EDGE,"E11.sketch_text.stroke-122"),sQuery(id+"F0.wireOp",EDGE,"E11.sketch_text.stroke-123"),sQuery(id+"F0.wireOp",EDGE,"E11.sketch_text.stroke-124"),sQuery(id+"F0.wireOp",EDGE,"E11.sketch_text.stroke-125"),sQuery(id+"F0.wireOp",EDGE,"E11.sketch_text.stroke-126"),sQuery(id+"F0.wireOp",EDGE,"E11.sketch_text.stroke-127"),sQuery(id+"F0.wireOp",EDGE,"E11.sketch_text.stroke-128"),sQuery(id+"F0.wireOp",EDGE,"E11.sketch_text.stroke-129"),sQuery(id+"F0.wireOp",EDGE,"E11.sketch_text.stroke-130"),sQuery(id+"F0.wireOp",EDGE,"E11.sketch_text.stroke-131"),sQuery(id+"F0.wireOp",EDGE,"E11.sketch_text.stroke-132"),sQuery(id+"F0.wireOp",EDGE,"E11.sketch_text.stroke-133"),sQuery(id+"F0.wireOp",EDGE,"E11.sketch_text.stroke-134"),sQuery(id+"F0.wireOp",EDGE,"E11.sketch_text.stroke-135"),sQuery(id+"F0.wireOp",EDGE,"E11.sketch_text.stroke-136"),sQuery(id+"F0.wireOp",EDGE,"E12.bottom"),subQ1,sQuery(id+"F0.wireOp",EDGE,"E12.left"),subQ0,sQuery(id+"F0.wireOp",EDGE,"E13")])],"isStart":false})],"blendedInto":[makeQuery(id+"F1.opExtrude","CAP_FACE",FACE,{"disambiguationData":[OSD([sQuery(id+"F0.wireOp",EDGE,"E0"),sQuery(id+"F0.wireOp",EDGE,"E2"),sQuery(id+"F0.wireOp",EDGE,"E3"),sQuery(id+"F0.wireOp",EDGE,"E4"),sQuery(id+"F0.wireOp",EDGE,"E6.MirrorCS"),sQuery(id+"F0.wireOp",EDGE,"E7.MirrorCS"),sQuery(id+"F0.wireOp",EDGE,"E9.MirrorCS"),sQuery(id+"F0.wireOp",EDGE,"E10.MirrorCS"),sQuery(id+"F0.wireOp",EDGE,"E11.sketch_text.stroke-0"),sQuery(id+"F0.wireOp",EDGE,"E11.sketch_text.stroke-1"),sQuery(id+"F0.wireOp",EDGE,"E11.sketch_text.stroke-2"),sQuery(id+"F0.wireOp",EDGE,"E11.sketch_text.stroke-3"),sQuery(id+"F0.wireOp",EDGE,"E11.sketch_text.stroke-4"),sQuery(id+"F0.wireOp",EDGE,"E11.sketch_text.stroke-5"),sQuery(id+"F0.wireOp",EDGE,"E11.sketch_text.stroke-6"),sQuery(id+"F0.wireOp",EDGE,"E11.sketch_text.stroke-7"),sQuery(id+"F0.wireOp",EDGE,"E11.sketch_text.stroke-8"),sQuery(id+"F0.wireOp",EDGE,"E11.sketch_text.stroke-9"),sQuery(id+"F0.wireOp",EDGE,"E11.sketch_text.stroke-10"),sQuery(id+"F0.wireOp",EDGE,"E11.sketch_text.stroke-11"),sQuery(id+"F0.wireOp",EDGE,"E11.sketch_text.stroke-12"),sQuery(id+"F0.wireOp",EDGE,"E11.sketch_text.stroke-13"),sQuery(id+"F0.wireOp",EDGE,"E11.sketch_text.stroke-14"),sQuery(id+"F0.wireOp",EDGE,"E11.sketch_text.stroke-15"),sQuery(id+"F0.wireOp",EDGE,"E11.sketch_text.stroke-16"),sQuery(id+"F0.wireOp",EDGE,"E11.sketch_text.stroke-17"),sQuery(id+"F0.wireOp",EDGE,"E11.sketch_text.stroke-18"),sQuery(id+"F0.wireOp",EDGE,"E11.sketch_text.stroke-19"),sQuery(id+"F0.wireOp",EDGE,"E11.sketch_text.stroke-20"),sQuery(id+"F0.wireOp",EDGE,"E11.sketch_text.stroke-21"),sQuery(id+"F0.wireOp",EDGE,"E11.sketch_text.stroke-22"),sQuery(id+"F0.wireOp",EDGE,"E11.sketch_text.stroke-23"),sQuery(id+"F0.wireOp",EDGE,"E11.sketch_text.stroke-24"),sQuery(id+"F0.wireOp",EDGE,"E11.sketch_text.stroke-25"),sQuery(id+"F0.wireOp",EDGE,"E11.sketch_text.stroke-26"),sQuery(id+"F0.wireOp",EDGE,"E11.sketch_text.stroke-27"),sQuery(id+"F0.wireOp",EDGE,"E11.sketch_text.stroke-28"),sQuery(id+"F0.wireOp",EDGE,"E11.sketch_text.stroke-29"),sQuery(id+"F0.wireOp",EDGE,"E11.sketch_text.stroke-30"),sQuery(id+"F0.wireOp",EDGE,"E11.sketch_text.stroke-31"),sQuery(id+"F0.wireOp",EDGE,"E11.sketch_text.stroke-32"),sQuery(id+"F0.wireOp",EDGE,"E11.sketch_text.stroke-33"),sQuery(id+"F0.wireOp",EDGE,"E11.sketch_text.stroke-34"),sQuery(id+"F0.wireOp",EDGE,"E11.sketch_text.stroke-35"),sQuery(id+"F0.wireOp",EDGE,"E11.sketch_text.stroke-36"),sQuery(id+"F0.wireOp",EDGE,"E11.sketch_text.stroke-37"),sQuery(id+"F0.wireOp",EDGE,"E11.sketch_text.stroke-38"),sQuery(id+"F0.wireOp",EDGE,"E11.sketch_text.stroke-39"),sQuery(id+"F0.wireOp",EDGE,"E11.sketch_text.stroke-40"),sQuery(id+"F0.wireOp",EDGE,"E11.sketch_text.stroke-41"),sQuery(id+"F0.wireOp",EDGE,"E11.sketch_text.stroke-42"),sQuery(id+"F0.wireOp",EDGE,"E11.sketch_text.stroke-43"),sQuery(id+"F0.wireOp",EDGE,"E11.sketch_text.stroke-44"),sQuery(id+"F0.wireOp",EDGE,"E11.sketch_text.stroke-45"),sQuery(id+"F0.wireOp",EDGE,"E11.sketch_text.stroke-46"),sQuery(id+"F0.wireOp",EDGE,"E11.sketch_text.stroke-47"),sQuery(id+"F0.wireOp",EDGE,"E11.sketch_text.stroke-48"),sQuery(id+"F0.wireOp",EDGE,"E11.sketch_text.stroke-49"),sQuery(id+"F0.wireOp",EDGE,"E11.sketch_text.stroke-50"),sQuery(id+"F0.wireOp",EDGE,"E11.sketch_text.stroke-51"),sQuery(id+"F0.wireOp",EDGE,"E11.sketch_text.stroke-52"),sQuery(id+"F0.wireOp",EDGE,"E11.sketch_text.stroke-53"),sQuery(id+"F0.wireOp",EDGE,"E11.sketch_text.stroke-54"),sQuery(id+"F0.wireOp",EDGE,"E11.sketch_text.stroke-55"),sQuery(id+"F0.wireOp",EDGE,"E11.sketch_text.stroke-56"),sQuery(id+"F0.wireOp",EDGE,"E11.sketch_text.stroke-57"),sQuery(id+"F0.wireOp",EDGE,"E11.sketch_text.stroke-58"),sQuery(id+"F0.wireOp",EDGE,"E11.sketch_text.stroke-59"),sQuery(id+"F0.wireOp",EDGE,"E11.sketch_text.stroke-60"),sQuery(id+"F0.wireOp",EDGE,"E11.sketch_text.stroke-61"),sQuery(id+"F0.wireOp",EDGE,"E11.sketch_text.stroke-62"),sQuery(id+"F0.wireOp",EDGE,"E11.sketch_text.stroke-63"),sQuery(id+"F0.wireOp",EDGE,"E11.sketch_text.stroke-64"),sQuery(id+"F0.wireOp",EDGE,"E11.sketch_text.stroke-65"),sQuery(id+"F0.wireOp",EDGE,"E11.sketch_text.stroke-66"),sQuery(id+"F0.wireOp",EDGE,"E11.sketch_text.stroke-67"),sQuery(id+"F0.wireOp",EDGE,"E11.sketch_text.stroke-68"),sQuery(id+"F0.wireOp",EDGE,"E11.sketch_text.stroke-74"),sQuery(id+"F0.wireOp",EDGE,"E11.sketch_text.stroke-75"),sQuery(id+"F0.wireOp",EDGE,"E11.sketch_text.stroke-76"),sQuery(id+"F0.wireOp",EDGE,"E11.sketch_text.stroke-77"),sQuery(id+"F0.wireOp",EDGE,"E11.sketch_text.stroke-78"),sQuery(id+"F0.wireOp",EDGE,"E11.sketch_text.stroke-79"),sQuery(id+"F0.wireOp",EDGE,"E11.sketch_text.stroke-80"),sQuery(id+"F0.wireOp",EDGE,"E11.sketch_text.stroke-81"),sQuery(id+"F0.wireOp",EDGE,"E11.sketch_text.stroke-82"),sQuery(id+"F0.wireOp",EDGE,"E11.sketch_text.stroke-83"),sQuery(id+"F0.wireOp",EDGE,"E11.sketch_text.stroke-84"),sQuery(id+"F0.wireOp",EDGE,"E11.sketch_text.stroke-85"),sQuery(id+"F0.wireOp",EDGE,"E11.sketch_text.stroke-86"),sQuery(id+"F0.wireOp",EDGE,"E11.sketch_text.stroke-87"),sQuery(id+"F0.wireOp",EDGE,"E11.sketch_text.stroke-88"),sQuery(id+"F0.wireOp",EDGE,"E11.sketch_text.stroke-89"),sQuery(id+"F0.wireOp",EDGE,"E11.sketch_text.stroke-104"),sQuery(id+"F0.wireOp",EDGE,"E11.sketch_text.stroke-105"),sQuery(id+"F0.wireOp",EDGE,"E11.sketch_text.stroke-106"),sQuery(id+"F0.wireOp",EDGE,"E11.sketch_text.stroke-107"),sQuery(id+"F0.wireOp",EDGE,"E11.sketch_text.stroke-108"),sQuery(id+"F0.wireOp",EDGE,"E11.sketch_text.stroke-109"),sQuery(id+"F0.wireOp",EDGE,"E11.sketch_text.stroke-110"),sQuery(id+"F0.wireOp",EDGE,"E11.sketch_text.stroke-111"),sQuery(id+"F0.wireOp",EDGE,"E11.sketch_text.stroke-112"),sQuery(id+"F0.wireOp",EDGE,"E11.sketch_text.stroke-113"),sQuery(id+"F0.wireOp",EDGE,"E11.sketch_text.stroke-114"),sQuery(id+"F0.wireOp",EDGE,"E11.sketch_text.stroke-115"),sQuery(id+"F0.wireOp",EDGE,"E11.sketch_text.stroke-116"),sQuery(id+"F0.wireOp",EDGE,"E11.sketch_text.stroke-117"),sQuery(id+"F0.wireOp",EDGE,"E11.sketch_text.stroke-118"),sQuery(id+"F0.wireOp",EDGE,"E11.sketch_text.stroke-119"),sQuery(id+"F0.wireOp",EDGE,"E11.sketch_text.stroke-120"),sQuery(id+"F0.wireOp",EDGE,"E11.sketch_text.stroke-121"),sQuery(id+"F0.wireOp",EDGE,"E11.sketch_text.stroke-122"),sQuery(id+"F0.wireOp",EDGE,"E11.sketch_text.stroke-123"),sQuery(id+"F0.wireOp",EDGE,"E11.sketch_text.stroke-124"),sQuery(id+"F0.wireOp",EDGE,"E11.sketch_text.stroke-125"),sQuery(id+"F0.wireOp",EDGE,"E11.sketch_text.stroke-126"),sQuery(id+"F0.wireOp",EDGE,"E11.sketch_text.stroke-127"),sQuery(id+"F0.wireOp",EDGE,"E11.sketch_text.stroke-128"),sQuery(id+"F0.wireOp",EDGE,"E11.sketch_text.stroke-129"),sQuery(id+"F0.wireOp",EDGE,"E11.sketch_text.stroke-130"),sQuery(id+"F0.wireOp",EDGE,"E11.sketch_text.stroke-131"),sQuery(id+"F0.wireOp",EDGE,"E11.sketch_text.stroke-132"),sQuery(id+"F0.wireOp",EDGE,"E11.sketch_text.stroke-133"),sQuery(id+"F0.wireOp",EDGE,"E11.sketch_text.stroke-134"),sQuery(id+"F0.wireOp",EDGE,"E11.sketch_text.stroke-135"),sQuery(id+"F0.wireOp",EDGE,"E11.sketch_text.stroke-136"),sQuery(id+"F0.wireOp",EDGE,"E12.bottom"),subQ1,sQuery(id+"F0.wireOp",EDGE,"E12.left"),subQ0,sQuery(id+"F0.wireOp",EDGE,"E13")])],"isStart":false})]});}
            var Q7;
            Q7=makeQuery(id+"F1.opExtrude","CAP_EDGE",EDGE,{"disambiguationData":[OSD([sQuery(id+"F0.wireOp",EDGE,"E12.right")])],"isStart":false});
            var Q8;
            {var subQ0=sQuery(id+"F0.wireOp",EDGE,"E12.right");var subQ1=sQuery(id+"F0.wireOp",EDGE,"E12.bottom");Q8=makeQuery(id+"F3.opFillet","BLEND_EDGE",EDGE,{"blendedFrom":[makeQuery(id+"F1.opExtrude","SWEPT_EDGE",EDGE,{"disambiguationData":[OSD([subQ1,subQ0])]}),makeQuery(id+"F1.opExtrude","CAP_FACE",FACE,{"disambiguationData":[OSD([sQuery(id+"F0.wireOp",EDGE,"E0"),sQuery(id+"F0.wireOp",EDGE,"E2"),sQuery(id+"F0.wireOp",EDGE,"E3"),sQuery(id+"F0.wireOp",EDGE,"E4"),sQuery(id+"F0.wireOp",EDGE,"E6.MirrorCS"),sQuery(id+"F0.wireOp",EDGE,"E7.MirrorCS"),sQuery(id+"F0.wireOp",EDGE,"E9.MirrorCS"),sQuery(id+"F0.wireOp",EDGE,"E10.MirrorCS"),sQuery(id+"F0.wireOp",EDGE,"E11.sketch_text.stroke-0"),sQuery(id+"F0.wireOp",EDGE,"E11.sketch_text.stroke-1"),sQuery(id+"F0.wireOp",EDGE,"E11.sketch_text.stroke-2"),sQuery(id+"F0.wireOp",EDGE,"E11.sketch_text.stroke-3"),sQuery(id+"F0.wireOp",EDGE,"E11.sketch_text.stroke-4"),sQuery(id+"F0.wireOp",EDGE,"E11.sketch_text.stroke-5"),sQuery(id+"F0.wireOp",EDGE,"E11.sketch_text.stroke-6"),sQuery(id+"F0.wireOp",EDGE,"E11.sketch_text.stroke-7"),sQuery(id+"F0.wireOp",EDGE,"E11.sketch_text.stroke-8"),sQuery(id+"F0.wireOp",EDGE,"E11.sketch_text.stroke-9"),sQuery(id+"F0.wireOp",EDGE,"E11.sketch_text.stroke-10"),sQuery(id+"F0.wireOp",EDGE,"E11.sketch_text.stroke-11"),sQuery(id+"F0.wireOp",EDGE,"E11.sketch_text.stroke-12"),sQuery(id+"F0.wireOp",EDGE,"E11.sketch_text.stroke-13"),sQuery(id+"F0.wireOp",EDGE,"E11.sketch_text.stroke-14"),sQuery(id+"F0.wireOp",EDGE,"E11.sketch_text.stroke-15"),sQuery(id+"F0.wireOp",EDGE,"E11.sketch_text.stroke-16"),sQuery(id+"F0.wireOp",EDGE,"E11.sketch_text.stroke-17"),sQuery(id+"F0.wireOp",EDGE,"E11.sketch_text.stroke-18"),sQuery(id+"F0.wireOp",EDGE,"E11.sketch_text.stroke-19"),sQuery(id+"F0.wireOp",EDGE,"E11.sketch_text.stroke-20"),sQuery(id+"F0.wireOp",EDGE,"E11.sketch_text.stroke-21"),sQuery(id+"F0.wireOp",EDGE,"E11.sketch_text.stroke-22"),sQuery(id+"F0.wireOp",EDGE,"E11.sketch_text.stroke-23"),sQuery(id+"F0.wireOp",EDGE,"E11.sketch_text.stroke-24"),sQuery(id+"F0.wireOp",EDGE,"E11.sketch_text.stroke-25"),sQuery(id+"F0.wireOp",EDGE,"E11.sketch_text.stroke-26"),sQuery(id+"F0.wireOp",EDGE,"E11.sketch_text.stroke-27"),sQuery(id+"F0.wireOp",EDGE,"E11.sketch_text.stroke-28"),sQuery(id+"F0.wireOp",EDGE,"E11.sketch_text.stroke-29"),sQuery(id+"F0.wireOp",EDGE,"E11.sketch_text.stroke-30"),sQuery(id+"F0.wireOp",EDGE,"E11.sketch_text.stroke-31"),sQuery(id+"F0.wireOp",EDGE,"E11.sketch_text.stroke-32"),sQuery(id+"F0.wireOp",EDGE,"E11.sketch_text.stroke-33"),sQuery(id+"F0.wireOp",EDGE,"E11.sketch_text.stroke-34"),sQuery(id+"F0.wireOp",EDGE,"E11.sketch_text.stroke-35"),sQuery(id+"F0.wireOp",EDGE,"E11.sketch_text.stroke-36"),sQuery(id+"F0.wireOp",EDGE,"E11.sketch_text.stroke-37"),sQuery(id+"F0.wireOp",EDGE,"E11.sketch_text.stroke-38"),sQuery(id+"F0.wireOp",EDGE,"E11.sketch_text.stroke-39"),sQuery(id+"F0.wireOp",EDGE,"E11.sketch_text.stroke-40"),sQuery(id+"F0.wireOp",EDGE,"E11.sketch_text.stroke-41"),sQuery(id+"F0.wireOp",EDGE,"E11.sketch_text.stroke-42"),sQuery(id+"F0.wireOp",EDGE,"E11.sketch_text.stroke-43"),sQuery(id+"F0.wireOp",EDGE,"E11.sketch_text.stroke-44"),sQuery(id+"F0.wireOp",EDGE,"E11.sketch_text.stroke-45"),sQuery(id+"F0.wireOp",EDGE,"E11.sketch_text.stroke-46"),sQuery(id+"F0.wireOp",EDGE,"E11.sketch_text.stroke-47"),sQuery(id+"F0.wireOp",EDGE,"E11.sketch_text.stroke-48"),sQuery(id+"F0.wireOp",EDGE,"E11.sketch_text.stroke-49"),sQuery(id+"F0.wireOp",EDGE,"E11.sketch_text.stroke-50"),sQuery(id+"F0.wireOp",EDGE,"E11.sketch_text.stroke-51"),sQuery(id+"F0.wireOp",EDGE,"E11.sketch_text.stroke-52"),sQuery(id+"F0.wireOp",EDGE,"E11.sketch_text.stroke-53"),sQuery(id+"F0.wireOp",EDGE,"E11.sketch_text.stroke-54"),sQuery(id+"F0.wireOp",EDGE,"E11.sketch_text.stroke-55"),sQuery(id+"F0.wireOp",EDGE,"E11.sketch_text.stroke-56"),sQuery(id+"F0.wireOp",EDGE,"E11.sketch_text.stroke-57"),sQuery(id+"F0.wireOp",EDGE,"E11.sketch_text.stroke-58"),sQuery(id+"F0.wireOp",EDGE,"E11.sketch_text.stroke-59"),sQuery(id+"F0.wireOp",EDGE,"E11.sketch_text.stroke-60"),sQuery(id+"F0.wireOp",EDGE,"E11.sketch_text.stroke-61"),sQuery(id+"F0.wireOp",EDGE,"E11.sketch_text.stroke-62"),sQuery(id+"F0.wireOp",EDGE,"E11.sketch_text.stroke-63"),sQuery(id+"F0.wireOp",EDGE,"E11.sketch_text.stroke-64"),sQuery(id+"F0.wireOp",EDGE,"E11.sketch_text.stroke-65"),sQuery(id+"F0.wireOp",EDGE,"E11.sketch_text.stroke-66"),sQuery(id+"F0.wireOp",EDGE,"E11.sketch_text.stroke-67"),sQuery(id+"F0.wireOp",EDGE,"E11.sketch_text.stroke-68"),sQuery(id+"F0.wireOp",EDGE,"E11.sketch_text.stroke-74"),sQuery(id+"F0.wireOp",EDGE,"E11.sketch_text.stroke-75"),sQuery(id+"F0.wireOp",EDGE,"E11.sketch_text.stroke-76"),sQuery(id+"F0.wireOp",EDGE,"E11.sketch_text.stroke-77"),sQuery(id+"F0.wireOp",EDGE,"E11.sketch_text.stroke-78"),sQuery(id+"F0.wireOp",EDGE,"E11.sketch_text.stroke-79"),sQuery(id+"F0.wireOp",EDGE,"E11.sketch_text.stroke-80"),sQuery(id+"F0.wireOp",EDGE,"E11.sketch_text.stroke-81"),sQuery(id+"F0.wireOp",EDGE,"E11.sketch_text.stroke-82"),sQuery(id+"F0.wireOp",EDGE,"E11.sketch_text.stroke-83"),sQuery(id+"F0.wireOp",EDGE,"E11.sketch_text.stroke-84"),sQuery(id+"F0.wireOp",EDGE,"E11.sketch_text.stroke-85"),sQuery(id+"F0.wireOp",EDGE,"E11.sketch_text.stroke-86"),sQuery(id+"F0.wireOp",EDGE,"E11.sketch_text.stroke-87"),sQuery(id+"F0.wireOp",EDGE,"E11.sketch_text.stroke-88"),sQuery(id+"F0.wireOp",EDGE,"E11.sketch_text.stroke-89"),sQuery(id+"F0.wireOp",EDGE,"E11.sketch_text.stroke-104"),sQuery(id+"F0.wireOp",EDGE,"E11.sketch_text.stroke-105"),sQuery(id+"F0.wireOp",EDGE,"E11.sketch_text.stroke-106"),sQuery(id+"F0.wireOp",EDGE,"E11.sketch_text.stroke-107"),sQuery(id+"F0.wireOp",EDGE,"E11.sketch_text.stroke-108"),sQuery(id+"F0.wireOp",EDGE,"E11.sketch_text.stroke-109"),sQuery(id+"F0.wireOp",EDGE,"E11.sketch_text.stroke-110"),sQuery(id+"F0.wireOp",EDGE,"E11.sketch_text.stroke-111"),sQuery(id+"F0.wireOp",EDGE,"E11.sketch_text.stroke-112"),sQuery(id+"F0.wireOp",EDGE,"E11.sketch_text.stroke-113"),sQuery(id+"F0.wireOp",EDGE,"E11.sketch_text.stroke-114"),sQuery(id+"F0.wireOp",EDGE,"E11.sketch_text.stroke-115"),sQuery(id+"F0.wireOp",EDGE,"E11.sketch_text.stroke-116"),sQuery(id+"F0.wireOp",EDGE,"E11.sketch_text.stroke-117"),sQuery(id+"F0.wireOp",EDGE,"E11.sketch_text.stroke-118"),sQuery(id+"F0.wireOp",EDGE,"E11.sketch_text.stroke-119"),sQuery(id+"F0.wireOp",EDGE,"E11.sketch_text.stroke-120"),sQuery(id+"F0.wireOp",EDGE,"E11.sketch_text.stroke-121"),sQuery(id+"F0.wireOp",EDGE,"E11.sketch_text.stroke-122"),sQuery(id+"F0.wireOp",EDGE,"E11.sketch_text.stroke-123"),sQuery(id+"F0.wireOp",EDGE,"E11.sketch_text.stroke-124"),sQuery(id+"F0.wireOp",EDGE,"E11.sketch_text.stroke-125"),sQuery(id+"F0.wireOp",EDGE,"E11.sketch_text.stroke-126"),sQuery(id+"F0.wireOp",EDGE,"E11.sketch_text.stroke-127"),sQuery(id+"F0.wireOp",EDGE,"E11.sketch_text.stroke-128"),sQuery(id+"F0.wireOp",EDGE,"E11.sketch_text.stroke-129"),sQuery(id+"F0.wireOp",EDGE,"E11.sketch_text.stroke-130"),sQuery(id+"F0.wireOp",EDGE,"E11.sketch_text.stroke-131"),sQuery(id+"F0.wireOp",EDGE,"E11.sketch_text.stroke-132"),sQuery(id+"F0.wireOp",EDGE,"E11.sketch_text.stroke-133"),sQuery(id+"F0.wireOp",EDGE,"E11.sketch_text.stroke-134"),sQuery(id+"F0.wireOp",EDGE,"E11.sketch_text.stroke-135"),sQuery(id+"F0.wireOp",EDGE,"E11.sketch_text.stroke-136"),subQ1,sQuery(id+"F0.wireOp",EDGE,"E12.top"),sQuery(id+"F0.wireOp",EDGE,"E12.left"),subQ0,sQuery(id+"F0.wireOp",EDGE,"E13")])],"isStart":false})],"blendedInto":[makeQuery(id+"F1.opExtrude","CAP_FACE",FACE,{"disambiguationData":[OSD([sQuery(id+"F0.wireOp",EDGE,"E0"),sQuery(id+"F0.wireOp",EDGE,"E2"),sQuery(id+"F0.wireOp",EDGE,"E3"),sQuery(id+"F0.wireOp",EDGE,"E4"),sQuery(id+"F0.wireOp",EDGE,"E6.MirrorCS"),sQuery(id+"F0.wireOp",EDGE,"E7.MirrorCS"),sQuery(id+"F0.wireOp",EDGE,"E9.MirrorCS"),sQuery(id+"F0.wireOp",EDGE,"E10.MirrorCS"),sQuery(id+"F0.wireOp",EDGE,"E11.sketch_text.stroke-0"),sQuery(id+"F0.wireOp",EDGE,"E11.sketch_text.stroke-1"),sQuery(id+"F0.wireOp",EDGE,"E11.sketch_text.stroke-2"),sQuery(id+"F0.wireOp",EDGE,"E11.sketch_text.stroke-3"),sQuery(id+"F0.wireOp",EDGE,"E11.sketch_text.stroke-4"),sQuery(id+"F0.wireOp",EDGE,"E11.sketch_text.stroke-5"),sQuery(id+"F0.wireOp",EDGE,"E11.sketch_text.stroke-6"),sQuery(id+"F0.wireOp",EDGE,"E11.sketch_text.stroke-7"),sQuery(id+"F0.wireOp",EDGE,"E11.sketch_text.stroke-8"),sQuery(id+"F0.wireOp",EDGE,"E11.sketch_text.stroke-9"),sQuery(id+"F0.wireOp",EDGE,"E11.sketch_text.stroke-10"),sQuery(id+"F0.wireOp",EDGE,"E11.sketch_text.stroke-11"),sQuery(id+"F0.wireOp",EDGE,"E11.sketch_text.stroke-12"),sQuery(id+"F0.wireOp",EDGE,"E11.sketch_text.stroke-13"),sQuery(id+"F0.wireOp",EDGE,"E11.sketch_text.stroke-14"),sQuery(id+"F0.wireOp",EDGE,"E11.sketch_text.stroke-15"),sQuery(id+"F0.wireOp",EDGE,"E11.sketch_text.stroke-16"),sQuery(id+"F0.wireOp",EDGE,"E11.sketch_text.stroke-17"),sQuery(id+"F0.wireOp",EDGE,"E11.sketch_text.stroke-18"),sQuery(id+"F0.wireOp",EDGE,"E11.sketch_text.stroke-19"),sQuery(id+"F0.wireOp",EDGE,"E11.sketch_text.stroke-20"),sQuery(id+"F0.wireOp",EDGE,"E11.sketch_text.stroke-21"),sQuery(id+"F0.wireOp",EDGE,"E11.sketch_text.stroke-22"),sQuery(id+"F0.wireOp",EDGE,"E11.sketch_text.stroke-23"),sQuery(id+"F0.wireOp",EDGE,"E11.sketch_text.stroke-24"),sQuery(id+"F0.wireOp",EDGE,"E11.sketch_text.stroke-25"),sQuery(id+"F0.wireOp",EDGE,"E11.sketch_text.stroke-26"),sQuery(id+"F0.wireOp",EDGE,"E11.sketch_text.stroke-27"),sQuery(id+"F0.wireOp",EDGE,"E11.sketch_text.stroke-28"),sQuery(id+"F0.wireOp",EDGE,"E11.sketch_text.stroke-29"),sQuery(id+"F0.wireOp",EDGE,"E11.sketch_text.stroke-30"),sQuery(id+"F0.wireOp",EDGE,"E11.sketch_text.stroke-31"),sQuery(id+"F0.wireOp",EDGE,"E11.sketch_text.stroke-32"),sQuery(id+"F0.wireOp",EDGE,"E11.sketch_text.stroke-33"),sQuery(id+"F0.wireOp",EDGE,"E11.sketch_text.stroke-34"),sQuery(id+"F0.wireOp",EDGE,"E11.sketch_text.stroke-35"),sQuery(id+"F0.wireOp",EDGE,"E11.sketch_text.stroke-36"),sQuery(id+"F0.wireOp",EDGE,"E11.sketch_text.stroke-37"),sQuery(id+"F0.wireOp",EDGE,"E11.sketch_text.stroke-38"),sQuery(id+"F0.wireOp",EDGE,"E11.sketch_text.stroke-39"),sQuery(id+"F0.wireOp",EDGE,"E11.sketch_text.stroke-40"),sQuery(id+"F0.wireOp",EDGE,"E11.sketch_text.stroke-41"),sQuery(id+"F0.wireOp",EDGE,"E11.sketch_text.stroke-42"),sQuery(id+"F0.wireOp",EDGE,"E11.sketch_text.stroke-43"),sQuery(id+"F0.wireOp",EDGE,"E11.sketch_text.stroke-44"),sQuery(id+"F0.wireOp",EDGE,"E11.sketch_text.stroke-45"),sQuery(id+"F0.wireOp",EDGE,"E11.sketch_text.stroke-46"),sQuery(id+"F0.wireOp",EDGE,"E11.sketch_text.stroke-47"),sQuery(id+"F0.wireOp",EDGE,"E11.sketch_text.stroke-48"),sQuery(id+"F0.wireOp",EDGE,"E11.sketch_text.stroke-49"),sQuery(id+"F0.wireOp",EDGE,"E11.sketch_text.stroke-50"),sQuery(id+"F0.wireOp",EDGE,"E11.sketch_text.stroke-51"),sQuery(id+"F0.wireOp",EDGE,"E11.sketch_text.stroke-52"),sQuery(id+"F0.wireOp",EDGE,"E11.sketch_text.stroke-53"),sQuery(id+"F0.wireOp",EDGE,"E11.sketch_text.stroke-54"),sQuery(id+"F0.wireOp",EDGE,"E11.sketch_text.stroke-55"),sQuery(id+"F0.wireOp",EDGE,"E11.sketch_text.stroke-56"),sQuery(id+"F0.wireOp",EDGE,"E11.sketch_text.stroke-57"),sQuery(id+"F0.wireOp",EDGE,"E11.sketch_text.stroke-58"),sQuery(id+"F0.wireOp",EDGE,"E11.sketch_text.stroke-59"),sQuery(id+"F0.wireOp",EDGE,"E11.sketch_text.stroke-60"),sQuery(id+"F0.wireOp",EDGE,"E11.sketch_text.stroke-61"),sQuery(id+"F0.wireOp",EDGE,"E11.sketch_text.stroke-62"),sQuery(id+"F0.wireOp",EDGE,"E11.sketch_text.stroke-63"),sQuery(id+"F0.wireOp",EDGE,"E11.sketch_text.stroke-64"),sQuery(id+"F0.wireOp",EDGE,"E11.sketch_text.stroke-65"),sQuery(id+"F0.wireOp",EDGE,"E11.sketch_text.stroke-66"),sQuery(id+"F0.wireOp",EDGE,"E11.sketch_text.stroke-67"),sQuery(id+"F0.wireOp",EDGE,"E11.sketch_text.stroke-68"),sQuery(id+"F0.wireOp",EDGE,"E11.sketch_text.stroke-74"),sQuery(id+"F0.wireOp",EDGE,"E11.sketch_text.stroke-75"),sQuery(id+"F0.wireOp",EDGE,"E11.sketch_text.stroke-76"),sQuery(id+"F0.wireOp",EDGE,"E11.sketch_text.stroke-77"),sQuery(id+"F0.wireOp",EDGE,"E11.sketch_text.stroke-78"),sQuery(id+"F0.wireOp",EDGE,"E11.sketch_text.stroke-79"),sQuery(id+"F0.wireOp",EDGE,"E11.sketch_text.stroke-80"),sQuery(id+"F0.wireOp",EDGE,"E11.sketch_text.stroke-81"),sQuery(id+"F0.wireOp",EDGE,"E11.sketch_text.stroke-82"),sQuery(id+"F0.wireOp",EDGE,"E11.sketch_text.stroke-83"),sQuery(id+"F0.wireOp",EDGE,"E11.sketch_text.stroke-84"),sQuery(id+"F0.wireOp",EDGE,"E11.sketch_text.stroke-85"),sQuery(id+"F0.wireOp",EDGE,"E11.sketch_text.stroke-86"),sQuery(id+"F0.wireOp",EDGE,"E11.sketch_text.stroke-87"),sQuery(id+"F0.wireOp",EDGE,"E11.sketch_text.stroke-88"),sQuery(id+"F0.wireOp",EDGE,"E11.sketch_text.stroke-89"),sQuery(id+"F0.wireOp",EDGE,"E11.sketch_text.stroke-104"),sQuery(id+"F0.wireOp",EDGE,"E11.sketch_text.stroke-105"),sQuery(id+"F0.wireOp",EDGE,"E11.sketch_text.stroke-106"),sQuery(id+"F0.wireOp",EDGE,"E11.sketch_text.stroke-107"),sQuery(id+"F0.wireOp",EDGE,"E11.sketch_text.stroke-108"),sQuery(id+"F0.wireOp",EDGE,"E11.sketch_text.stroke-109"),sQuery(id+"F0.wireOp",EDGE,"E11.sketch_text.stroke-110"),sQuery(id+"F0.wireOp",EDGE,"E11.sketch_text.stroke-111"),sQuery(id+"F0.wireOp",EDGE,"E11.sketch_text.stroke-112"),sQuery(id+"F0.wireOp",EDGE,"E11.sketch_text.stroke-113"),sQuery(id+"F0.wireOp",EDGE,"E11.sketch_text.stroke-114"),sQuery(id+"F0.wireOp",EDGE,"E11.sketch_text.stroke-115"),sQuery(id+"F0.wireOp",EDGE,"E11.sketch_text.stroke-116"),sQuery(id+"F0.wireOp",EDGE,"E11.sketch_text.stroke-117"),sQuery(id+"F0.wireOp",EDGE,"E11.sketch_text.stroke-118"),sQuery(id+"F0.wireOp",EDGE,"E11.sketch_text.stroke-119"),sQuery(id+"F0.wireOp",EDGE,"E11.sketch_text.stroke-120"),sQuery(id+"F0.wireOp",EDGE,"E11.sketch_text.stroke-121"),sQuery(id+"F0.wireOp",EDGE,"E11.sketch_text.stroke-122"),sQuery(id+"F0.wireOp",EDGE,"E11.sketch_text.stroke-123"),sQuery(id+"F0.wireOp",EDGE,"E11.sketch_text.stroke-124"),sQuery(id+"F0.wireOp",EDGE,"E11.sketch_text.stroke-125"),sQuery(id+"F0.wireOp",EDGE,"E11.sketch_text.stroke-126"),sQuery(id+"F0.wireOp",EDGE,"E11.sketch_text.stroke-127"),sQuery(id+"F0.wireOp",EDGE,"E11.sketch_text.stroke-128"),sQuery(id+"F0.wireOp",EDGE,"E11.sketch_text.stroke-129"),sQuery(id+"F0.wireOp",EDGE,"E11.sketch_text.stroke-130"),sQuery(id+"F0.wireOp",EDGE,"E11.sketch_text.stroke-131"),sQuery(id+"F0.wireOp",EDGE,"E11.sketch_text.stroke-132"),sQuery(id+"F0.wireOp",EDGE,"E11.sketch_text.stroke-133"),sQuery(id+"F0.wireOp",EDGE,"E11.sketch_text.stroke-134"),sQuery(id+"F0.wireOp",EDGE,"E11.sketch_text.stroke-135"),sQuery(id+"F0.wireOp",EDGE,"E11.sketch_text.stroke-136"),subQ1,sQuery(id+"F0.wireOp",EDGE,"E12.top"),sQuery(id+"F0.wireOp",EDGE,"E12.left"),subQ0,sQuery(id+"F0.wireOp",EDGE,"E13")])],"isStart":false})]});}
            fillet(context, id + "F4", {"entities" : qUnion([Q0, Q1, Q2, Q3, Q4, Q5, Q6, Q7, Q8]), "radius" : 1 * mm, "tangentPropagation" : true, "allowEdgeOverflow" : false});
        }
        {
            var Q0;
            {var subQ0=sQuery(id+"F0.wireOp",EDGE,"E11.sketch_text.stroke-136");var subQ1=sQuery(id+"F0.wireOp",EDGE,"E11.sketch_text.stroke-135");var subQ2=sQuery(id+"F0.wireOp",EDGE,"E11.sketch_text.stroke-134");var subQ3=sQuery(id+"F0.wireOp",EDGE,"E11.sketch_text.stroke-133");var subQ4=sQuery(id+"F0.wireOp",EDGE,"E11.sketch_text.stroke-132");var subQ5=sQuery(id+"F0.wireOp",EDGE,"E11.sketch_text.stroke-131");var subQ6=sQuery(id+"F0.wireOp",EDGE,"E11.sketch_text.stroke-130");var subQ7=sQuery(id+"F0.wireOp",EDGE,"E11.sketch_text.stroke-129");var subQ8=sQuery(id+"F0.wireOp",EDGE,"E11.sketch_text.stroke-128");var subQ9=sQuery(id+"F0.wireOp",EDGE,"E11.sketch_text.stroke-127");var subQ10=sQuery(id+"F0.wireOp",EDGE,"E11.sketch_text.stroke-126");var subQ11=sQuery(id+"F0.wireOp",EDGE,"E11.sketch_text.stroke-125");var subQ12=sQuery(id+"F0.wireOp",EDGE,"E11.sketch_text.stroke-124");var subQ13=sQuery(id+"F0.wireOp",EDGE,"E11.sketch_text.stroke-123");var subQ14=sQuery(id+"F0.wireOp",EDGE,"E11.sketch_text.stroke-122");var subQ15=sQuery(id+"F0.wireOp",EDGE,"E11.sketch_text.stroke-121");var subQ16=sQuery(id+"F0.wireOp",EDGE,"E11.sketch_text.stroke-120");var subQ17=sQuery(id+"F0.wireOp",EDGE,"E11.sketch_text.stroke-119");var subQ18=sQuery(id+"F0.wireOp",EDGE,"E11.sketch_text.stroke-118");var subQ19=sQuery(id+"F0.wireOp",EDGE,"E11.sketch_text.stroke-117");var subQ20=sQuery(id+"F0.wireOp",EDGE,"E11.sketch_text.stroke-116");var subQ21=sQuery(id+"F0.wireOp",EDGE,"E11.sketch_text.stroke-115");var subQ22=sQuery(id+"F0.wireOp",EDGE,"E11.sketch_text.stroke-114");var subQ23=sQuery(id+"F0.wireOp",EDGE,"E11.sketch_text.stroke-113");var subQ24=sQuery(id+"F0.wireOp",EDGE,"E11.sketch_text.stroke-112");var subQ25=sQuery(id+"F0.wireOp",EDGE,"E11.sketch_text.stroke-111");var subQ26=sQuery(id+"F0.wireOp",EDGE,"E11.sketch_text.stroke-110");var subQ27=sQuery(id+"F0.wireOp",EDGE,"E11.sketch_text.stroke-109");var subQ28=sQuery(id+"F0.wireOp",EDGE,"E11.sketch_text.stroke-108");var subQ29=sQuery(id+"F0.wireOp",EDGE,"E11.sketch_text.stroke-107");var subQ30=sQuery(id+"F0.wireOp",EDGE,"E11.sketch_text.stroke-106");var subQ31=sQuery(id+"F0.wireOp",EDGE,"E11.sketch_text.stroke-105");var subQ32=sQuery(id+"F0.wireOp",EDGE,"E11.sketch_text.stroke-104");var subQ33=sQuery(id+"F0.wireOp",EDGE,"E11.sketch_text.stroke-103");var subQ34=sQuery(id+"F0.wireOp",EDGE,"E11.sketch_text.stroke-102");var subQ35=sQuery(id+"F0.wireOp",EDGE,"E11.sketch_text.stroke-101");var subQ36=sQuery(id+"F0.wireOp",EDGE,"E11.sketch_text.stroke-100");var subQ37=sQuery(id+"F0.wireOp",EDGE,"E11.sketch_text.stroke-99");var subQ38=sQuery(id+"F0.wireOp",EDGE,"E11.sketch_text.stroke-98");var subQ39=sQuery(id+"F0.wireOp",EDGE,"E11.sketch_text.stroke-97");var subQ40=sQuery(id+"F0.wireOp",EDGE,"E11.sketch_text.stroke-96");var subQ41=sQuery(id+"F0.wireOp",EDGE,"E11.sketch_text.stroke-95");var subQ42=sQuery(id+"F0.wireOp",EDGE,"E11.sketch_text.stroke-94");var subQ43=sQuery(id+"F0.wireOp",EDGE,"E11.sketch_text.stroke-93");var subQ44=sQuery(id+"F0.wireOp",EDGE,"E11.sketch_text.stroke-92");var subQ45=sQuery(id+"F0.wireOp",EDGE,"E11.sketch_text.stroke-91");var subQ46=sQuery(id+"F0.wireOp",EDGE,"E11.sketch_text.stroke-90");var subQ47=sQuery(id+"F0.wireOp",EDGE,"E11.sketch_text.stroke-89");var subQ48=sQuery(id+"F0.wireOp",EDGE,"E11.sketch_text.stroke-88");var subQ49=sQuery(id+"F0.wireOp",EDGE,"E11.sketch_text.stroke-87");var subQ50=sQuery(id+"F0.wireOp",EDGE,"E11.sketch_text.stroke-86");var subQ51=sQuery(id+"F0.wireOp",EDGE,"E11.sketch_text.stroke-85");var subQ52=sQuery(id+"F0.wireOp",EDGE,"E11.sketch_text.stroke-84");var subQ53=sQuery(id+"F0.wireOp",EDGE,"E11.sketch_text.stroke-83");var subQ54=sQuery(id+"F0.wireOp",EDGE,"E11.sketch_text.stroke-82");var subQ55=sQuery(id+"F0.wireOp",EDGE,"E11.sketch_text.stroke-81");var subQ56=sQuery(id+"F0.wireOp",EDGE,"E11.sketch_text.stroke-80");var subQ57=sQuery(id+"F0.wireOp",EDGE,"E11.sketch_text.stroke-79");var subQ58=sQuery(id+"F0.wireOp",EDGE,"E11.sketch_text.stroke-78");var subQ59=sQuery(id+"F0.wireOp",EDGE,"E11.sketch_text.stroke-77");var subQ60=sQuery(id+"F0.wireOp",EDGE,"E11.sketch_text.stroke-76");var subQ61=sQuery(id+"F0.wireOp",EDGE,"E11.sketch_text.stroke-75");var subQ62=sQuery(id+"F0.wireOp",EDGE,"E11.sketch_text.stroke-74");var subQ63=sQuery(id+"F0.wireOp",EDGE,"E11.sketch_text.stroke-73");var subQ64=sQuery(id+"F0.wireOp",EDGE,"E11.sketch_text.stroke-72");var subQ65=sQuery(id+"F0.wireOp",EDGE,"E11.sketch_text.stroke-71");var subQ66=sQuery(id+"F0.wireOp",EDGE,"E11.sketch_text.stroke-70");var subQ67=sQuery(id+"F0.wireOp",EDGE,"E11.sketch_text.stroke-69");var subQ68=sQuery(id+"F0.wireOp",EDGE,"E11.sketch_text.stroke-68");var subQ69=sQuery(id+"F0.wireOp",EDGE,"E11.sketch_text.stroke-67");var subQ70=sQuery(id+"F0.wireOp",EDGE,"E11.sketch_text.stroke-66");var subQ71=sQuery(id+"F0.wireOp",EDGE,"E11.sketch_text.stroke-65");var subQ72=sQuery(id+"F0.wireOp",EDGE,"E11.sketch_text.stroke-64");var subQ73=sQuery(id+"F0.wireOp",EDGE,"E11.sketch_text.stroke-63");var subQ74=sQuery(id+"F0.wireOp",EDGE,"E11.sketch_text.stroke-62");var subQ75=sQuery(id+"F0.wireOp",EDGE,"E11.sketch_text.stroke-61");var subQ76=sQuery(id+"F0.wireOp",EDGE,"E11.sketch_text.stroke-60");var subQ77=sQuery(id+"F0.wireOp",EDGE,"E11.sketch_text.stroke-59");var subQ78=sQuery(id+"F0.wireOp",EDGE,"E11.sketch_text.stroke-58");var subQ79=sQuery(id+"F0.wireOp",EDGE,"E11.sketch_text.stroke-57");var subQ80=sQuery(id+"F0.wireOp",EDGE,"E11.sketch_text.stroke-56");var subQ81=sQuery(id+"F0.wireOp",EDGE,"E11.sketch_text.stroke-55");var subQ82=sQuery(id+"F0.wireOp",EDGE,"E11.sketch_text.stroke-54");var subQ83=sQuery(id+"F0.wireOp",EDGE,"E11.sketch_text.stroke-53");var subQ84=sQuery(id+"F0.wireOp",EDGE,"E11.sketch_text.stroke-52");var subQ85=sQuery(id+"F0.wireOp",EDGE,"E11.sketch_text.stroke-51");var subQ86=sQuery(id+"F0.wireOp",EDGE,"E11.sketch_text.stroke-50");var subQ87=sQuery(id+"F0.wireOp",EDGE,"E11.sketch_text.stroke-49");var subQ88=sQuery(id+"F0.wireOp",EDGE,"E11.sketch_text.stroke-48");var subQ89=sQuery(id+"F0.wireOp",EDGE,"E11.sketch_text.stroke-47");var subQ90=sQuery(id+"F0.wireOp",EDGE,"E11.sketch_text.stroke-46");var subQ91=sQuery(id+"F0.wireOp",EDGE,"E11.sketch_text.stroke-45");var subQ92=sQuery(id+"F0.wireOp",EDGE,"E11.sketch_text.stroke-44");var subQ93=sQuery(id+"F0.wireOp",EDGE,"E11.sketch_text.stroke-43");var subQ94=sQuery(id+"F0.wireOp",EDGE,"E11.sketch_text.stroke-42");var subQ95=sQuery(id+"F0.wireOp",EDGE,"E11.sketch_text.stroke-41");var subQ96=sQuery(id+"F0.wireOp",EDGE,"E11.sketch_text.stroke-40");var subQ97=sQuery(id+"F0.wireOp",EDGE,"E11.sketch_text.stroke-39");var subQ98=sQuery(id+"F0.wireOp",EDGE,"E11.sketch_text.stroke-38");var subQ99=sQuery(id+"F0.wireOp",EDGE,"E11.sketch_text.stroke-37");var subQ100=sQuery(id+"F0.wireOp",EDGE,"E11.sketch_text.stroke-36");var subQ101=sQuery(id+"F0.wireOp",EDGE,"E11.sketch_text.stroke-35");var subQ102=sQuery(id+"F0.wireOp",EDGE,"E11.sketch_text.stroke-34");var subQ103=sQuery(id+"F0.wireOp",EDGE,"E11.sketch_text.stroke-33");var subQ104=sQuery(id+"F0.wireOp",EDGE,"E11.sketch_text.stroke-32");var subQ105=sQuery(id+"F0.wireOp",EDGE,"E11.sketch_text.stroke-31");var subQ106=sQuery(id+"F0.wireOp",EDGE,"E11.sketch_text.stroke-30");var subQ107=sQuery(id+"F0.wireOp",EDGE,"E11.sketch_text.stroke-29");var subQ108=sQuery(id+"F0.wireOp",EDGE,"E11.sketch_text.stroke-28");var subQ109=sQuery(id+"F0.wireOp",EDGE,"E11.sketch_text.stroke-27");var subQ110=sQuery(id+"F0.wireOp",EDGE,"E11.sketch_text.stroke-26");var subQ111=sQuery(id+"F0.wireOp",EDGE,"E11.sketch_text.stroke-25");var subQ112=sQuery(id+"F0.wireOp",EDGE,"E11.sketch_text.stroke-24");var subQ113=sQuery(id+"F0.wireOp",EDGE,"E11.sketch_text.stroke-23");var subQ114=sQuery(id+"F0.wireOp",EDGE,"E11.sketch_text.stroke-22");var subQ115=sQuery(id+"F0.wireOp",EDGE,"E11.sketch_text.stroke-21");var subQ116=sQuery(id+"F0.wireOp",EDGE,"E11.sketch_text.stroke-20");var subQ117=sQuery(id+"F0.wireOp",EDGE,"E11.sketch_text.stroke-19");var subQ118=sQuery(id+"F0.wireOp",EDGE,"E11.sketch_text.stroke-18");var subQ119=sQuery(id+"F0.wireOp",EDGE,"E11.sketch_text.stroke-17");var subQ120=sQuery(id+"F0.wireOp",EDGE,"E11.sketch_text.stroke-16");var subQ121=sQuery(id+"F0.wireOp",EDGE,"E11.sketch_text.stroke-15");var subQ122=sQuery(id+"F0.wireOp",EDGE,"E11.sketch_text.stroke-14");var subQ123=sQuery(id+"F0.wireOp",EDGE,"E11.sketch_text.stroke-13");var subQ124=sQuery(id+"F0.wireOp",EDGE,"E11.sketch_text.stroke-12");var subQ125=sQuery(id+"F0.wireOp",EDGE,"E11.sketch_text.stroke-11");var subQ126=sQuery(id+"F0.wireOp",EDGE,"E11.sketch_text.stroke-10");var subQ127=sQuery(id+"F0.wireOp",EDGE,"E11.sketch_text.stroke-9");var subQ128=sQuery(id+"F0.wireOp",EDGE,"E11.sketch_text.stroke-8");var subQ129=sQuery(id+"F0.wireOp",EDGE,"E11.sketch_text.stroke-7");var subQ130=sQuery(id+"F0.wireOp",EDGE,"E11.sketch_text.stroke-6");var subQ131=sQuery(id+"F0.wireOp",EDGE,"E11.sketch_text.stroke-5");var subQ132=sQuery(id+"F0.wireOp",EDGE,"E11.sketch_text.stroke-4");var subQ133=sQuery(id+"F0.wireOp",EDGE,"E11.sketch_text.stroke-3");var subQ134=sQuery(id+"F0.wireOp",EDGE,"E11.sketch_text.stroke-2");var subQ135=sQuery(id+"F0.wireOp",EDGE,"E11.sketch_text.stroke-1");var subQ136=sQuery(id+"F0.wireOp",EDGE,"E11.sketch_text.stroke-0");var subQ137=sQuery(id+"F0.wireOp",EDGE,"E10.MirrorCS");var subQ138=sQuery(id+"F0.wireOp",EDGE,"E9.MirrorCS");var subQ139=sQuery(id+"F0.wireOp",EDGE,"E8.MirrorC");var subQ140=sQuery(id+"F0.wireOp",EDGE,"E7.MirrorCS");var subQ141=sQuery(id+"F0.wireOp",EDGE,"E6.MirrorCS");var subQ142=sQuery(id+"F0.wireOp",EDGE,"E5");var subQ143=sQuery(id+"F0.wireOp",EDGE,"E4");var subQ144=sQuery(id+"F0.wireOp",EDGE,"E3");var subQ145=sQuery(id+"F0.wireOp",EDGE,"E2");var subQ146=sQuery(id+"F0.wireOp",EDGE,"E0");Q0=makeQuery(id+"F2.boolean.opBoolean","MERGE",FACE,{"derivedFrom":[makeQuery(id+"F1.opExtrude","CAP_FACE",FACE,{"disambiguationData":[OSD([subQ146,subQ145,subQ144,subQ143,subQ141,subQ140,subQ138,subQ137,subQ136,subQ135,subQ134,subQ133,subQ132,subQ131,subQ130,subQ129,subQ128,subQ127,subQ126,subQ125,subQ124,subQ123,subQ122,subQ121,subQ120,subQ119,subQ118,subQ117,subQ116,subQ115,subQ114,subQ113,subQ112,subQ111,subQ110,subQ109,subQ108,subQ107,subQ106,subQ105,subQ104,subQ103,subQ102,subQ101,subQ100,subQ99,subQ98,subQ97,subQ96,subQ95,subQ94,subQ93,subQ92,subQ91,subQ90,subQ89,subQ88,subQ87,subQ86,subQ85,subQ84,subQ83,subQ82,subQ81,subQ80,subQ79,subQ78,subQ77,subQ76,subQ75,subQ74,subQ73,subQ72,subQ71,subQ70,subQ69,subQ68,subQ62,subQ61,subQ60,subQ59,subQ58,subQ57,subQ56,subQ55,subQ54,subQ53,subQ52,subQ51,subQ50,subQ49,subQ48,subQ47,subQ32,subQ31,subQ30,subQ29,subQ28,subQ27,subQ26,subQ25,subQ24,subQ23,subQ22,subQ21,subQ20,subQ19,subQ18,subQ17,subQ16,subQ15,subQ14,subQ13,subQ12,subQ11,subQ10,subQ9,subQ8,subQ7,subQ6,subQ5,subQ4,subQ3,subQ2,subQ1,subQ0,sQuery(id+"F0.wireOp",EDGE,"E12.bottom"),sQuery(id+"F0.wireOp",EDGE,"E12.top"),sQuery(id+"F0.wireOp",EDGE,"E12.left"),sQuery(id+"F0.wireOp",EDGE,"E12.right"),sQuery(id+"F0.wireOp",EDGE,"E13")])],"isStart":true}),makeQuery(id+"F1.opExtrude","CAP_FACE",FACE,{"disambiguationData":[OSD([subQ142])],"isStart":true}),makeQuery(id+"F1.opExtrude","CAP_FACE",FACE,{"disambiguationData":[OSD([subQ139])],"isStart":true}),makeQuery(id+"F1.opExtrude","CAP_FACE",FACE,{"disambiguationData":[OSD([subQ67,subQ66,subQ65,subQ64,subQ63])],"isStart":true}),makeQuery(id+"F1.opExtrude","CAP_FACE",FACE,{"disambiguationData":[OSD([subQ46,subQ45,subQ44,subQ43,subQ42,subQ41,subQ40])],"isStart":true}),makeQuery(id+"F1.opExtrude","CAP_FACE",FACE,{"disambiguationData":[OSD([subQ39,subQ38,subQ37,subQ36,subQ35,subQ34,subQ33])],"isStart":true}),makeQuery(id+"F2.opExtrude","CAP_FACE",FACE,{"disambiguationData":[OSD([subQ146,subQ145,subQ144,subQ143,subQ142,subQ141,subQ140,subQ139,subQ138,subQ137])],"isStart":true}),makeQuery(id+"F2.opExtrude","CAP_FACE",FACE,{"disambiguationData":[OSD([subQ136,subQ135,subQ134,subQ133,subQ132,subQ131,subQ130,subQ129,subQ128,subQ127,subQ126,subQ125,subQ124,subQ123,subQ122,subQ121,subQ120,subQ119,subQ118,subQ117,subQ116,subQ115,subQ114,subQ113,subQ112,subQ111,subQ110,subQ109,subQ108,subQ107,subQ106])],"isStart":true}),makeQuery(id+"F2.opExtrude","CAP_FACE",FACE,{"disambiguationData":[OSD([subQ105,subQ104,subQ103,subQ102,subQ101,subQ100,subQ99,subQ98,subQ97,subQ96,subQ95,subQ94,subQ93,subQ92,subQ91,subQ90,subQ89,subQ88,subQ87,subQ86,subQ85,subQ84,subQ83])],"isStart":true}),makeQuery(id+"F2.opExtrude","CAP_FACE",FACE,{"disambiguationData":[OSD([subQ82,subQ81,subQ80,subQ79,subQ78,subQ77,subQ76,subQ75,subQ74,subQ73,subQ72,subQ71,subQ70,subQ69,subQ68,subQ67,subQ66,subQ65,subQ64,subQ63])],"isStart":true}),makeQuery(id+"F2.opExtrude","CAP_FACE",FACE,{"disambiguationData":[OSD([subQ62,subQ61,subQ60,subQ59,subQ58,subQ57,subQ56,subQ55,subQ54,subQ53,subQ52,subQ51,subQ50,subQ49,subQ48,subQ47,subQ46,subQ45,subQ44,subQ43,subQ42,subQ41,subQ40,subQ39,subQ38,subQ37,subQ36,subQ35,subQ34,subQ33])],"isStart":true}),makeQuery(id+"F2.opExtrude","CAP_FACE",FACE,{"disambiguationData":[OSD([subQ32,subQ31,subQ30,subQ29,subQ28,subQ27,subQ26,subQ25,subQ24,subQ23,subQ22,subQ21,subQ20,subQ19,subQ18,subQ17,subQ16,subQ15,subQ14,subQ13,subQ12,subQ11,subQ10])],"isStart":true}),makeQuery(id+"F2.opExtrude","CAP_FACE",FACE,{"disambiguationData":[OSD([subQ9,subQ8,subQ7,subQ6,subQ5,subQ4,subQ3,subQ2,subQ1,subQ0])],"isStart":true})]});}
            var sketch = newSketch(context, id + "F5", { "sketchPlane" : qUnion([Q0])});
            skText(sketch, "E14", { "text": "Orphan\nBlack", "fontName": "Arimo-Bold.ttf"});
            skLineSegment(sketch, "E15", {"start": v(7.5, 20.46) * mm, "end": v(0, 20.46) * mm, "construction": true});
            skLineSegment(sketch, "E16", {"start": v(7.5, 20.46) * mm, "end": v(7.5, 14.54) * mm, "construction": true});
            skLineSegment(sketch, "E17", {"start": v(42.5, 20.46) * mm, "end": v(50, 20.46) * mm, "construction": true});
            skLineSegment(sketch, "E18", {"start": v(7.5, 27.54) * mm, "end": v(7.5, 44.54) * mm, "construction": true});
            const initialGuessF5  = {"E14": [0.0425, 0.02754, -1, 0, 0.00707]};
            skSetInitialGuess(sketch, initialGuessF5);
            skSolve(sketch);
        }
        {
            var Q0;
            Q0=makeQuery(id+"F5.imprint","IMPRINT",FACE,{"disambiguationData":[TD([[makeQuery(id+"F5.imprint","IMPRINT",EDGE,{"derivedFrom":sQuery(id+"F5.wireOp",EDGE,"E14.sketch_text.stroke-34")}),-1.0]])]});
            var Q1;
            Q1=makeQuery(id+"F5.imprint","IMPRINT",FACE,{"disambiguationData":[TD([[makeQuery(id+"F5.imprint","IMPRINT",EDGE,{"derivedFrom":sQuery(id+"F5.wireOp",EDGE,"E14.sketch_text.stroke-17")}),-1.0]])]});
            var Q2;
            Q2=makeQuery(id+"F5.imprint","IMPRINT",FACE,{"disambiguationData":[TD([[makeQuery(id+"F5.imprint","IMPRINT",EDGE,{"derivedFrom":sQuery(id+"F5.wireOp",EDGE,"E14.sketch_text.stroke-0")}),-1.0]])]});
            var Q3;
            Q3=makeQuery(id+"F5.imprint","IMPRINT",FACE,{"disambiguationData":[TD([[makeQuery(id+"F5.imprint","IMPRINT",EDGE,{"derivedFrom":sQuery(id+"F5.wireOp",EDGE,"E14.sketch_text.stroke-131")}),-1.0]])]});
            var Q4;
            Q4=makeQuery(id+"F5.imprint","IMPRINT",FACE,{"disambiguationData":[TD([[makeQuery(id+"F5.imprint","IMPRINT",EDGE,{"derivedFrom":sQuery(id+"F5.wireOp",EDGE,"E14.sketch_text.stroke-155")}),-1.0]])]});
            var Q5;
            Q5=makeQuery(id+"F5.imprint","IMPRINT",FACE,{"disambiguationData":[TD([[makeQuery(id+"F5.imprint","IMPRINT",EDGE,{"derivedFrom":sQuery(id+"F5.wireOp",EDGE,"E14.sketch_text.stroke-57")}),-1.0]])]});
            var Q6;
            Q6=makeQuery(id+"F5.imprint","IMPRINT",FACE,{"disambiguationData":[TD([[makeQuery(id+"F5.imprint","IMPRINT",EDGE,{"derivedFrom":sQuery(id+"F5.wireOp",EDGE,"E14.sketch_text.stroke-74")}),-1.0]])]});
            var Q7;
            Q7=makeQuery(id+"F5.imprint","IMPRINT",FACE,{"disambiguationData":[TD([[makeQuery(id+"F5.imprint","IMPRINT",EDGE,{"derivedFrom":sQuery(id+"F5.wireOp",EDGE,"E14.sketch_text.stroke-112")}),-1.0]])]});
            var Q8;
            Q8=makeQuery(id+"F5.imprint","IMPRINT",FACE,{"disambiguationData":[TD([[makeQuery(id+"F5.imprint","IMPRINT",EDGE,{"derivedFrom":sQuery(id+"F5.wireOp",EDGE,"E14.sketch_text.stroke-214")}),-1.0]])]});
            var Q9;
            Q9=makeQuery(id+"F5.imprint","IMPRINT",FACE,{"disambiguationData":[TD([[makeQuery(id+"F5.imprint","IMPRINT",EDGE,{"derivedFrom":sQuery(id+"F5.wireOp",EDGE,"E14.sketch_text.stroke-197")}),-1.0]])]});
            var Q10;
            Q10=makeQuery(id+"F5.imprint","IMPRINT",FACE,{"disambiguationData":[TD([[makeQuery(id+"F5.imprint","IMPRINT",EDGE,{"derivedFrom":sQuery(id+"F5.wireOp",EDGE,"E14.sketch_text.stroke-159")}),-1.0]])]});
            extrude(context, id + "F6", {"entities" : qUnion([Q0, Q1, Q2, Q3, Q4, Q5, Q6, Q7, Q8, Q9, Q10]), "operationType" : NewBodyOperationType.REMOVE, "oppositeDirection" : true, "depth" : 1 * mm, "offsetDistance" : 25 * mm});
        }
    });
